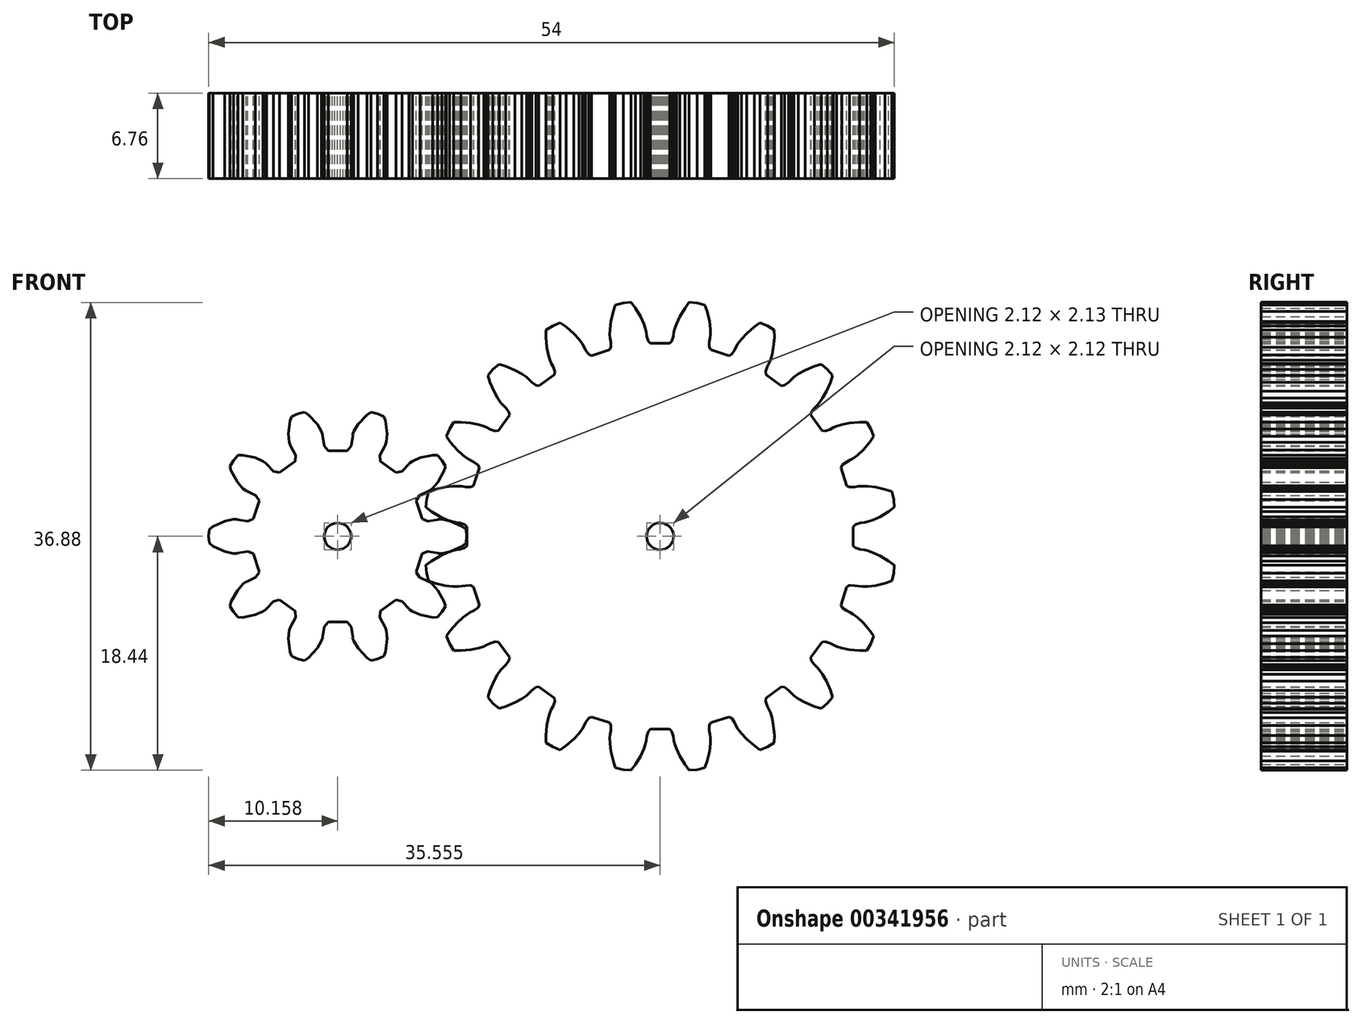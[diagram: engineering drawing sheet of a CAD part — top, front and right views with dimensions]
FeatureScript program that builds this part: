
annotation { "Feature Type Name" : "Feature", "Feature Type Description" : "" }
export const myFeature = defineFeature(function(context is Context, id is Id, definition is map)
    precondition{}
    {
        {
            var Q0;
            Q0=qCreatedBy(makeId("Front.planeOp"),FACE);
            var sketch = newSketch(context, id + "F0", { "sketchPlane" : qUnion([Q0])});
            skLineSegment(sketch, "E0", {"start": v(-16.87, -12) * mm, "end": v(-16.21, -11.23) * mm});
            skLineSegment(sketch, "E1", {"start": v(-16.21, -11.23) * mm, "end": v(-15.68, -10.36) * mm});
            skLineSegment(sketch, "E2", {"start": v(-15.68, -10.36) * mm, "end": v(-15.9, -9.67) * mm});
            skLineSegment(sketch, "E3", {"start": v(-15.9, -9.67) * mm, "end": v(-16.82, -8) * mm});
            skLineSegment(sketch, "E4", {"start": v(-16.82, -8) * mm, "end": v(-17.64, -7.07) * mm});
            skLineSegment(sketch, "E5", {"start": v(-17.64, -7.07) * mm, "end": v(-18.07, -6.75) * mm});
            skLineSegment(sketch, "E6", {"start": v(-18.07, -6.75) * mm, "end": v(-18.2, -6.72) * mm});
            skLineSegment(sketch, "E7", {"start": v(-18.2, -6.72) * mm, "end": v(-19.55, -6.05) * mm});
            skLineSegment(sketch, "E8", {"start": v(-19.55, -6.05) * mm, "end": v(-20.04, -5.27) * mm});
            skLineSegment(sketch, "E9", {"start": v(-20.04, -5.27) * mm, "end": v(-19.16, -2.57) * mm});
            skLineSegment(sketch, "E10", {"start": v(-19.16, -2.57) * mm, "end": v(-18.3, -2.22) * mm});
            skLineSegment(sketch, "E11", {"start": v(-18.3, -2.22) * mm, "end": v(-16.83, -2.48) * mm});
            skLineSegment(sketch, "E12", {"start": v(-16.83, -2.48) * mm, "end": v(-16.7, -2.53) * mm});
            skLineSegment(sketch, "E13", {"start": v(-16.7, -2.53) * mm, "end": v(-16.16, -2.52) * mm});
            skLineSegment(sketch, "E14", {"start": v(-16.16, -2.52) * mm, "end": v(-14.95, -2.24) * mm});
            skLineSegment(sketch, "E15", {"start": v(-14.95, -2.24) * mm, "end": v(-13.22, -1.44) * mm});
            skLineSegment(sketch, "E16", {"start": v(-13.22, -1.44) * mm, "end": v(-12.64, -1) * mm});
            skLineSegment(sketch, "E17", {"start": v(-12.64, -1) * mm, "end": v(-12.56, 0) * mm});
            skLineSegment(sketch, "E18", {"start": v(-12.56, 0) * mm, "end": v(-12.64, 1) * mm});
            skLineSegment(sketch, "E19", {"start": v(-12.64, 1) * mm, "end": v(-13.22, 1.44) * mm});
            skLineSegment(sketch, "E20", {"start": v(-13.22, 1.44) * mm, "end": v(-14.95, 2.24) * mm});
            skLineSegment(sketch, "E21", {"start": v(-14.95, 2.24) * mm, "end": v(-16.16, 2.52) * mm});
            skLineSegment(sketch, "E22", {"start": v(-16.16, 2.52) * mm, "end": v(-16.7, 2.53) * mm});
            skLineSegment(sketch, "E23", {"start": v(-16.7, 2.53) * mm, "end": v(-16.83, 2.48) * mm});
            skLineSegment(sketch, "E24", {"start": v(-16.83, 2.48) * mm, "end": v(-18.3, 2.22) * mm});
            skLineSegment(sketch, "E25", {"start": v(-18.3, 2.22) * mm, "end": v(-19.16, 2.57) * mm});
            skLineSegment(sketch, "E26", {"start": v(-19.16, 2.57) * mm, "end": v(-20.04, 5.27) * mm});
            skLineSegment(sketch, "E27", {"start": v(-20.04, 5.27) * mm, "end": v(-19.55, 6.05) * mm});
            skLineSegment(sketch, "E28", {"start": v(-19.55, 6.05) * mm, "end": v(-18.2, 6.72) * mm});
            skLineSegment(sketch, "E29", {"start": v(-18.2, 6.72) * mm, "end": v(-18.07, 6.75) * mm});
            skLineSegment(sketch, "E30", {"start": v(-18.07, 6.75) * mm, "end": v(-17.64, 7.07) * mm});
            skLineSegment(sketch, "E31", {"start": v(-17.64, 7.07) * mm, "end": v(-16.82, 8) * mm});
            skLineSegment(sketch, "E32", {"start": v(-16.82, 8) * mm, "end": v(-15.9, 9.67) * mm});
            skLineSegment(sketch, "E33", {"start": v(-15.9, 9.67) * mm, "end": v(-15.68, 10.36) * mm});
            skLineSegment(sketch, "E34", {"start": v(-15.68, 10.36) * mm, "end": v(-16.21, 11.23) * mm});
            skLineSegment(sketch, "E35", {"start": v(-16.21, 11.23) * mm, "end": v(-16.87, 12) * mm});
            skLineSegment(sketch, "E36", {"start": v(-16.87, 12) * mm, "end": v(-17.6, 12) * mm});
            skLineSegment(sketch, "E37", {"start": v(-17.6, 12) * mm, "end": v(-19.46, 11.64) * mm});
            skLineSegment(sketch, "E38", {"start": v(-19.46, 11.64) * mm, "end": v(-20.6, 11.15) * mm});
            skLineSegment(sketch, "E39", {"start": v(-20.6, 11.15) * mm, "end": v(-21.04, 10.84) * mm});
            skLineSegment(sketch, "E40", {"start": v(-21.04, 10.84) * mm, "end": v(-21.11, 10.72) * mm});
            skLineSegment(sketch, "E41", {"start": v(-21.11, 10.72) * mm, "end": v(-22.16, 9.65) * mm});
            skLineSegment(sketch, "E42", {"start": v(-22.16, 9.65) * mm, "end": v(-23.06, 9.43) * mm});
            skLineSegment(sketch, "E43", {"start": v(-23.06, 9.43) * mm, "end": v(-25.36, 11.1) * mm});
            skLineSegment(sketch, "E44", {"start": v(-25.36, 11.1) * mm, "end": v(-25.42, 12.02) * mm});
            skLineSegment(sketch, "E45", {"start": v(-25.42, 12.02) * mm, "end": v(-24.72, 13.35) * mm});
            skLineSegment(sketch, "E46", {"start": v(-24.72, 13.35) * mm, "end": v(-24.63, 13.45) * mm});
            skLineSegment(sketch, "E47", {"start": v(-24.63, 13.45) * mm, "end": v(-24.47, 13.96) * mm});
            skLineSegment(sketch, "E48", {"start": v(-24.47, 13.96) * mm, "end": v(-24.36, 15.2) * mm});
            skLineSegment(sketch, "E49", {"start": v(-24.36, 15.2) * mm, "end": v(-24.6, 17.1) * mm});
            skLineSegment(sketch, "E50", {"start": v(-24.6, 17.1) * mm, "end": v(-24.82, 17.78) * mm});
            skLineSegment(sketch, "E51", {"start": v(-24.82, 17.78) * mm, "end": v(-25.76, 18.16) * mm});
            skLineSegment(sketch, "E52", {"start": v(-25.76, 18.16) * mm, "end": v(-26.74, 18.4) * mm});
            skLineSegment(sketch, "E53", {"start": v(-26.74, 18.4) * mm, "end": v(-27.33, 17.98) * mm});
            skLineSegment(sketch, "E54", {"start": v(-27.33, 17.98) * mm, "end": v(-28.63, 16.59) * mm});
            skLineSegment(sketch, "E55", {"start": v(-28.63, 16.59) * mm, "end": v(-29.27, 15.52) * mm});
            skLineSegment(sketch, "E56", {"start": v(-29.27, 15.52) * mm, "end": v(-29.44, 15.01) * mm});
            skLineSegment(sketch, "E57", {"start": v(-29.44, 15.01) * mm, "end": v(-29.43, 14.88) * mm});
            skLineSegment(sketch, "E58", {"start": v(-29.43, 14.88) * mm, "end": v(-29.65, 13.4) * mm});
            skLineSegment(sketch, "E59", {"start": v(-29.65, 13.4) * mm, "end": v(-30.24, 12.68) * mm});
            skLineSegment(sketch, "E60", {"start": v(-30.24, 12.68) * mm, "end": v(-33.08, 12.68) * mm});
            skLineSegment(sketch, "E61", {"start": v(-33.08, 12.68) * mm, "end": v(-33.68, 13.4) * mm});
            skLineSegment(sketch, "E62", {"start": v(-33.68, 13.4) * mm, "end": v(-33.9, 14.88) * mm});
            skLineSegment(sketch, "E63", {"start": v(-33.9, 14.88) * mm, "end": v(-33.88, 15.01) * mm});
            skLineSegment(sketch, "E64", {"start": v(-33.88, 15.01) * mm, "end": v(-34.05, 15.52) * mm});
            skLineSegment(sketch, "E65", {"start": v(-34.05, 15.52) * mm, "end": v(-34.7, 16.59) * mm});
            skLineSegment(sketch, "E66", {"start": v(-34.7, 16.59) * mm, "end": v(-35.99, 17.98) * mm});
            skLineSegment(sketch, "E67", {"start": v(-35.99, 17.98) * mm, "end": v(-36.58, 18.4) * mm});
            skLineSegment(sketch, "E68", {"start": v(-36.58, 18.4) * mm, "end": v(-37.56, 18.16) * mm});
            skLineSegment(sketch, "E69", {"start": v(-37.56, 18.16) * mm, "end": v(-38.5, 17.78) * mm});
            skLineSegment(sketch, "E70", {"start": v(-38.5, 17.78) * mm, "end": v(-38.73, 17.1) * mm});
            skLineSegment(sketch, "E71", {"start": v(-38.73, 17.1) * mm, "end": v(-38.96, 15.2) * mm});
            skLineSegment(sketch, "E72", {"start": v(-38.96, 15.2) * mm, "end": v(-38.85, 13.96) * mm});
            skLineSegment(sketch, "E73", {"start": v(-38.85, 13.96) * mm, "end": v(-38.7, 13.45) * mm});
            skLineSegment(sketch, "E74", {"start": v(-38.7, 13.45) * mm, "end": v(-38.6, 13.35) * mm});
            skLineSegment(sketch, "E75", {"start": v(-38.6, 13.35) * mm, "end": v(-37.9, 12.02) * mm});
            skLineSegment(sketch, "E76", {"start": v(-37.9, 12.02) * mm, "end": v(-37.97, 11.1) * mm});
            skLineSegment(sketch, "E77", {"start": v(-37.97, 11.1) * mm, "end": v(-40.27, 9.43) * mm});
            skLineSegment(sketch, "E78", {"start": v(-40.27, 9.43) * mm, "end": v(-41.16, 9.65) * mm});
            skLineSegment(sketch, "E79", {"start": v(-41.16, 9.65) * mm, "end": v(-42.2, 10.72) * mm});
            skLineSegment(sketch, "E80", {"start": v(-42.2, 10.72) * mm, "end": v(-42.28, 10.84) * mm});
            skLineSegment(sketch, "E81", {"start": v(-42.28, 10.84) * mm, "end": v(-42.72, 11.15) * mm});
            skLineSegment(sketch, "E82", {"start": v(-42.72, 11.15) * mm, "end": v(-43.86, 11.64) * mm});
            skLineSegment(sketch, "E83", {"start": v(-43.86, 11.64) * mm, "end": v(-45.73, 12) * mm});
            skLineSegment(sketch, "E84", {"start": v(-45.73, 12) * mm, "end": v(-46.46, 12) * mm});
            skLineSegment(sketch, "E85", {"start": v(-46.46, 12) * mm, "end": v(-47.11, 11.23) * mm});
            skLineSegment(sketch, "E86", {"start": v(-47.11, 11.23) * mm, "end": v(-47.64, 10.36) * mm});
            skLineSegment(sketch, "E87", {"start": v(-47.64, 10.36) * mm, "end": v(-47.43, 9.67) * mm});
            skLineSegment(sketch, "E88", {"start": v(-47.43, 9.67) * mm, "end": v(-46.5, 8) * mm});
            skLineSegment(sketch, "E89", {"start": v(-46.5, 8) * mm, "end": v(-45.68, 7.07) * mm});
            skLineSegment(sketch, "E90", {"start": v(-45.68, 7.07) * mm, "end": v(-45.25, 6.75) * mm});
            skLineSegment(sketch, "E91", {"start": v(-45.25, 6.75) * mm, "end": v(-45.12, 6.72) * mm});
            skLineSegment(sketch, "E92", {"start": v(-45.12, 6.72) * mm, "end": v(-43.78, 6.05) * mm});
            skLineSegment(sketch, "E93", {"start": v(-43.78, 6.05) * mm, "end": v(-43.28, 5.27) * mm});
            skLineSegment(sketch, "E94", {"start": v(-43.28, 5.27) * mm, "end": v(-44.16, 2.57) * mm});
            skLineSegment(sketch, "E95", {"start": v(-44.16, 2.57) * mm, "end": v(-45.02, 2.22) * mm});
            skLineSegment(sketch, "E96", {"start": v(-45.02, 2.22) * mm, "end": v(-46.5, 2.48) * mm});
            skLineSegment(sketch, "E97", {"start": v(-46.5, 2.48) * mm, "end": v(-46.62, 2.53) * mm});
            skLineSegment(sketch, "E98", {"start": v(-46.62, 2.53) * mm, "end": v(-47.16, 2.52) * mm});
            skLineSegment(sketch, "E99", {"start": v(-47.16, 2.52) * mm, "end": v(-48.37, 2.24) * mm});
            skLineSegment(sketch, "E100", {"start": v(-48.37, 2.24) * mm, "end": v(-50.1, 1.44) * mm});
            skLineSegment(sketch, "E101", {"start": v(-50.1, 1.44) * mm, "end": v(-50.68, 1) * mm});
            skLineSegment(sketch, "E102", {"start": v(-50.68, 1) * mm, "end": v(-50.76, 0) * mm});
            skLineSegment(sketch, "E103", {"start": v(-50.76, 0) * mm, "end": v(-50.68, -1) * mm});
            skLineSegment(sketch, "E104", {"start": v(-50.68, -1) * mm, "end": v(-50.1, -1.44) * mm});
            skLineSegment(sketch, "E105", {"start": v(-50.1, -1.44) * mm, "end": v(-48.37, -2.24) * mm});
            skLineSegment(sketch, "E106", {"start": v(-48.37, -2.24) * mm, "end": v(-47.16, -2.52) * mm});
            skLineSegment(sketch, "E107", {"start": v(-47.16, -2.52) * mm, "end": v(-46.62, -2.53) * mm});
            skLineSegment(sketch, "E108", {"start": v(-46.62, -2.53) * mm, "end": v(-46.5, -2.48) * mm});
            skLineSegment(sketch, "E109", {"start": v(-46.5, -2.48) * mm, "end": v(-45.02, -2.22) * mm});
            skLineSegment(sketch, "E110", {"start": v(-45.02, -2.22) * mm, "end": v(-44.16, -2.57) * mm});
            skLineSegment(sketch, "E111", {"start": v(-44.16, -2.57) * mm, "end": v(-43.28, -5.27) * mm});
            skLineSegment(sketch, "E112", {"start": v(-43.28, -5.27) * mm, "end": v(-43.78, -6.05) * mm});
            skLineSegment(sketch, "E113", {"start": v(-43.78, -6.05) * mm, "end": v(-45.12, -6.72) * mm});
            skLineSegment(sketch, "E114", {"start": v(-45.12, -6.72) * mm, "end": v(-45.25, -6.75) * mm});
            skLineSegment(sketch, "E115", {"start": v(-45.25, -6.75) * mm, "end": v(-45.68, -7.07) * mm});
            skLineSegment(sketch, "E116", {"start": v(-45.68, -7.07) * mm, "end": v(-46.5, -8) * mm});
            skLineSegment(sketch, "E117", {"start": v(-46.5, -8) * mm, "end": v(-47.43, -9.67) * mm});
            skLineSegment(sketch, "E118", {"start": v(-47.43, -9.67) * mm, "end": v(-47.64, -10.36) * mm});
            skLineSegment(sketch, "E119", {"start": v(-47.64, -10.36) * mm, "end": v(-47.11, -11.23) * mm});
            skLineSegment(sketch, "E120", {"start": v(-47.11, -11.23) * mm, "end": v(-46.46, -12) * mm});
            skLineSegment(sketch, "E121", {"start": v(-46.46, -12) * mm, "end": v(-45.73, -12) * mm});
            skLineSegment(sketch, "E122", {"start": v(-45.73, -12) * mm, "end": v(-43.86, -11.64) * mm});
            skLineSegment(sketch, "E123", {"start": v(-43.86, -11.64) * mm, "end": v(-42.72, -11.15) * mm});
            skLineSegment(sketch, "E124", {"start": v(-42.72, -11.15) * mm, "end": v(-42.28, -10.84) * mm});
            skLineSegment(sketch, "E125", {"start": v(-42.28, -10.84) * mm, "end": v(-42.2, -10.72) * mm});
            skLineSegment(sketch, "E126", {"start": v(-42.2, -10.72) * mm, "end": v(-41.16, -9.65) * mm});
            skLineSegment(sketch, "E127", {"start": v(-41.16, -9.65) * mm, "end": v(-40.27, -9.43) * mm});
            skLineSegment(sketch, "E128", {"start": v(-40.27, -9.43) * mm, "end": v(-37.97, -11.1) * mm});
            skLineSegment(sketch, "E129", {"start": v(-37.97, -11.1) * mm, "end": v(-37.9, -12.02) * mm});
            skLineSegment(sketch, "E130", {"start": v(-37.9, -12.02) * mm, "end": v(-38.6, -13.35) * mm});
            skLineSegment(sketch, "E131", {"start": v(-38.6, -13.35) * mm, "end": v(-38.7, -13.45) * mm});
            skLineSegment(sketch, "E132", {"start": v(-38.7, -13.45) * mm, "end": v(-38.85, -13.96) * mm});
            skLineSegment(sketch, "E133", {"start": v(-38.85, -13.96) * mm, "end": v(-38.96, -15.2) * mm});
            skLineSegment(sketch, "E134", {"start": v(-38.96, -15.2) * mm, "end": v(-38.73, -17.1) * mm});
            skLineSegment(sketch, "E135", {"start": v(-38.73, -17.1) * mm, "end": v(-38.5, -17.78) * mm});
            skLineSegment(sketch, "E136", {"start": v(-38.5, -17.78) * mm, "end": v(-37.56, -18.16) * mm});
            skLineSegment(sketch, "E137", {"start": v(-37.56, -18.16) * mm, "end": v(-36.58, -18.4) * mm});
            skLineSegment(sketch, "E138", {"start": v(-36.58, -18.4) * mm, "end": v(-35.99, -17.98) * mm});
            skLineSegment(sketch, "E139", {"start": v(-35.99, -17.98) * mm, "end": v(-34.7, -16.59) * mm});
            skLineSegment(sketch, "E140", {"start": v(-34.7, -16.59) * mm, "end": v(-34.05, -15.52) * mm});
            skLineSegment(sketch, "E141", {"start": v(-34.05, -15.52) * mm, "end": v(-33.88, -15.01) * mm});
            skLineSegment(sketch, "E142", {"start": v(-33.88, -15.01) * mm, "end": v(-33.9, -14.88) * mm});
            skLineSegment(sketch, "E143", {"start": v(-33.9, -14.88) * mm, "end": v(-33.68, -13.4) * mm});
            skLineSegment(sketch, "E144", {"start": v(-33.68, -13.4) * mm, "end": v(-33.08, -12.68) * mm});
            skLineSegment(sketch, "E145", {"start": v(-33.08, -12.68) * mm, "end": v(-30.24, -12.68) * mm});
            skLineSegment(sketch, "E146", {"start": v(-30.24, -12.68) * mm, "end": v(-29.65, -13.4) * mm});
            skLineSegment(sketch, "E147", {"start": v(-29.65, -13.4) * mm, "end": v(-29.43, -14.88) * mm});
            skLineSegment(sketch, "E148", {"start": v(-29.43, -14.88) * mm, "end": v(-29.44, -15.01) * mm});
            skLineSegment(sketch, "E149", {"start": v(-29.44, -15.01) * mm, "end": v(-29.27, -15.52) * mm});
            skLineSegment(sketch, "E150", {"start": v(-29.27, -15.52) * mm, "end": v(-28.63, -16.59) * mm});
            skLineSegment(sketch, "E151", {"start": v(-28.63, -16.59) * mm, "end": v(-27.33, -17.98) * mm});
            skLineSegment(sketch, "E152", {"start": v(-27.33, -17.98) * mm, "end": v(-26.74, -18.4) * mm});
            skLineSegment(sketch, "E153", {"start": v(-26.74, -18.4) * mm, "end": v(-25.76, -18.16) * mm});
            skLineSegment(sketch, "E154", {"start": v(-25.76, -18.16) * mm, "end": v(-24.82, -17.78) * mm});
            skLineSegment(sketch, "E155", {"start": v(-24.82, -17.78) * mm, "end": v(-24.6, -17.1) * mm});
            skLineSegment(sketch, "E156", {"start": v(-24.6, -17.1) * mm, "end": v(-24.36, -15.2) * mm});
            skLineSegment(sketch, "E157", {"start": v(-24.36, -15.2) * mm, "end": v(-24.47, -13.96) * mm});
            skLineSegment(sketch, "E158", {"start": v(-24.47, -13.96) * mm, "end": v(-24.63, -13.45) * mm});
            skLineSegment(sketch, "E159", {"start": v(-24.63, -13.45) * mm, "end": v(-24.72, -13.35) * mm});
            skLineSegment(sketch, "E160", {"start": v(-24.72, -13.35) * mm, "end": v(-25.42, -12.02) * mm});
            skLineSegment(sketch, "E161", {"start": v(-25.42, -12.02) * mm, "end": v(-25.36, -11.1) * mm});
            skLineSegment(sketch, "E162", {"start": v(-25.36, -11.1) * mm, "end": v(-23.06, -9.43) * mm});
            skLineSegment(sketch, "E163", {"start": v(-23.06, -9.43) * mm, "end": v(-22.16, -9.65) * mm});
            skLineSegment(sketch, "E164", {"start": v(-22.16, -9.65) * mm, "end": v(-21.11, -10.72) * mm});
            skLineSegment(sketch, "E165", {"start": v(-21.11, -10.72) * mm, "end": v(-21.04, -10.84) * mm});
            skLineSegment(sketch, "E166", {"start": v(-21.04, -10.84) * mm, "end": v(-20.6, -11.15) * mm});
            skLineSegment(sketch, "E167", {"start": v(-20.6, -11.15) * mm, "end": v(-19.46, -11.64) * mm});
            skLineSegment(sketch, "E168", {"start": v(-19.46, -11.64) * mm, "end": v(-17.6, -12) * mm});
            skLineSegment(sketch, "E169", {"start": v(-17.6, -12) * mm, "end": v(-16.87, -12) * mm});
            skLineSegment(sketch, "E170", {"start": v(-31.25, -1.96) * mm, "end": v(-31.66, -2) * mm});
            skLineSegment(sketch, "E171", {"start": v(-31.66, -2) * mm, "end": v(-32.08, -1.96) * mm});
            skLineSegment(sketch, "E172", {"start": v(-32.08, -1.96) * mm, "end": v(-32.48, -1.83) * mm});
            skLineSegment(sketch, "E173", {"start": v(-32.48, -1.83) * mm, "end": v(-32.84, -1.62) * mm});
            skLineSegment(sketch, "E174", {"start": v(-32.84, -1.62) * mm, "end": v(-33.15, -1.34) * mm});
            skLineSegment(sketch, "E175", {"start": v(-33.15, -1.34) * mm, "end": v(-33.4, -1) * mm});
            skLineSegment(sketch, "E176", {"start": v(-33.4, -1) * mm, "end": v(-33.56, -0.62) * mm});
            skLineSegment(sketch, "E177", {"start": v(-33.56, -0.62) * mm, "end": v(-33.65, -0.2) * mm});
            skLineSegment(sketch, "E178", {"start": v(-33.65, -0.2) * mm, "end": v(-33.65, 0.2) * mm});
            skLineSegment(sketch, "E179", {"start": v(-33.65, 0.2) * mm, "end": v(-33.56, 0.62) * mm});
            skLineSegment(sketch, "E180", {"start": v(-33.56, 0.62) * mm, "end": v(-33.4, 1) * mm});
            skLineSegment(sketch, "E181", {"start": v(-33.4, 1) * mm, "end": v(-33.15, 1.34) * mm});
            skLineSegment(sketch, "E182", {"start": v(-33.15, 1.34) * mm, "end": v(-32.84, 1.62) * mm});
            skLineSegment(sketch, "E183", {"start": v(-32.84, 1.62) * mm, "end": v(-32.48, 1.83) * mm});
            skLineSegment(sketch, "E184", {"start": v(-32.48, 1.83) * mm, "end": v(-32.08, 1.96) * mm});
            skLineSegment(sketch, "E185", {"start": v(-32.08, 1.96) * mm, "end": v(-31.66, 2) * mm});
            skLineSegment(sketch, "E186", {"start": v(-31.66, 2) * mm, "end": v(-31.25, 1.96) * mm});
            skLineSegment(sketch, "E187", {"start": v(-31.25, 1.96) * mm, "end": v(-30.85, 1.83) * mm});
            skLineSegment(sketch, "E188", {"start": v(-30.85, 1.83) * mm, "end": v(-30.49, 1.62) * mm});
            skLineSegment(sketch, "E189", {"start": v(-30.49, 1.62) * mm, "end": v(-30.18, 1.34) * mm});
            skLineSegment(sketch, "E190", {"start": v(-30.18, 1.34) * mm, "end": v(-29.93, 1) * mm});
            skLineSegment(sketch, "E191", {"start": v(-29.93, 1) * mm, "end": v(-29.76, 0.62) * mm});
            skLineSegment(sketch, "E192", {"start": v(-29.76, 0.62) * mm, "end": v(-29.67, 0.2) * mm});
            skLineSegment(sketch, "E193", {"start": v(-29.67, 0.2) * mm, "end": v(-29.67, -0.2) * mm});
            skLineSegment(sketch, "E194", {"start": v(-29.67, -0.2) * mm, "end": v(-29.76, -0.62) * mm});
            skLineSegment(sketch, "E195", {"start": v(-29.76, -0.62) * mm, "end": v(-29.93, -1) * mm});
            skLineSegment(sketch, "E196", {"start": v(-29.93, -1) * mm, "end": v(-30.18, -1.34) * mm});
            skLineSegment(sketch, "E197", {"start": v(-30.18, -1.34) * mm, "end": v(-30.49, -1.62) * mm});
            skLineSegment(sketch, "E198", {"start": v(-30.49, -1.62) * mm, "end": v(-30.85, -1.83) * mm});
            skLineSegment(sketch, "E199", {"start": v(-30.85, -1.83) * mm, "end": v(-31.25, -1.96) * mm});
            skLineSegment(sketch, "E200", {"start": v(-18.22, 6.63) * mm, "end": v(-18.5, 5.48) * mm});
            skLineSegment(sketch, "E201", {"start": v(-18.5, 5.48) * mm, "end": v(-18.6, 4.3) * mm});
            skLineSegment(sketch, "E202", {"start": v(-18.6, 4.3) * mm, "end": v(-17.75, 3.67) * mm});
            skLineSegment(sketch, "E203", {"start": v(-17.75, 3.67) * mm, "end": v(-16.47, 2.9) * mm});
            skLineSegment(sketch, "E204", {"start": v(-16.47, 2.9) * mm, "end": v(-15.42, 2.41) * mm});
            skLineSegment(sketch, "E205", {"start": v(-15.42, 2.41) * mm, "end": v(-14.63, 2.15) * mm});
            skLineSegment(sketch, "E206", {"start": v(-14.63, 2.15) * mm, "end": v(-14.15, 2.03) * mm});
            skLineSegment(sketch, "E207", {"start": v(-14.15, 2.03) * mm, "end": v(-13.57, 1.96) * mm});
            skLineSegment(sketch, "E208", {"start": v(-13.57, 1.96) * mm, "end": v(-12.85, 1.74) * mm});
            skLineSegment(sketch, "E209", {"start": v(-12.85, 1.74) * mm, "end": v(-12.51, 1.42) * mm});
            skLineSegment(sketch, "E210", {"start": v(-12.51, 1.42) * mm, "end": v(-12.51, -1.42) * mm});
            skLineSegment(sketch, "E211", {"start": v(-12.51, -1.42) * mm, "end": v(-12.85, -1.74) * mm});
            skLineSegment(sketch, "E212", {"start": v(-12.85, -1.74) * mm, "end": v(-13.57, -1.96) * mm});
            skLineSegment(sketch, "E213", {"start": v(-13.57, -1.96) * mm, "end": v(-14.15, -2.03) * mm});
            skLineSegment(sketch, "E214", {"start": v(-14.15, -2.03) * mm, "end": v(-14.63, -2.15) * mm});
            skLineSegment(sketch, "E215", {"start": v(-14.63, -2.15) * mm, "end": v(-15.42, -2.41) * mm});
            skLineSegment(sketch, "E216", {"start": v(-15.42, -2.41) * mm, "end": v(-16.47, -2.9) * mm});
            skLineSegment(sketch, "E217", {"start": v(-16.47, -2.9) * mm, "end": v(-17.75, -3.67) * mm});
            skLineSegment(sketch, "E218", {"start": v(-17.75, -3.67) * mm, "end": v(-18.6, -4.3) * mm});
            skLineSegment(sketch, "E219", {"start": v(-18.6, -4.3) * mm, "end": v(-18.5, -5.48) * mm});
            skLineSegment(sketch, "E220", {"start": v(-18.5, -5.48) * mm, "end": v(-18.22, -6.63) * mm});
            skLineSegment(sketch, "E221", {"start": v(-18.22, -6.63) * mm, "end": v(-17.23, -6.97) * mm});
            skLineSegment(sketch, "E222", {"start": v(-17.23, -6.97) * mm, "end": v(-15.77, -7.3) * mm});
            skLineSegment(sketch, "E223", {"start": v(-15.77, -7.3) * mm, "end": v(-14.62, -7.44) * mm});
            skLineSegment(sketch, "E224", {"start": v(-14.62, -7.44) * mm, "end": v(-13.8, -7.45) * mm});
            skLineSegment(sketch, "E225", {"start": v(-13.8, -7.45) * mm, "end": v(-13.3, -7.4) * mm});
            skLineSegment(sketch, "E226", {"start": v(-13.3, -7.4) * mm, "end": v(-12.73, -7.3) * mm});
            skLineSegment(sketch, "E227", {"start": v(-12.73, -7.3) * mm, "end": v(-11.97, -7.29) * mm});
            skLineSegment(sketch, "E228", {"start": v(-11.97, -7.29) * mm, "end": v(-11.55, -7.49) * mm});
            skLineSegment(sketch, "E229", {"start": v(-11.55, -7.49) * mm, "end": v(-10.67, -10.19) * mm});
            skLineSegment(sketch, "E230", {"start": v(-10.67, -10.19) * mm, "end": v(-10.9, -10.6) * mm});
            skLineSegment(sketch, "E231", {"start": v(-10.9, -10.6) * mm, "end": v(-11.51, -11.03) * mm});
            skLineSegment(sketch, "E232", {"start": v(-11.51, -11.03) * mm, "end": v(-12.04, -11.28) * mm});
            skLineSegment(sketch, "E233", {"start": v(-12.04, -11.28) * mm, "end": v(-12.47, -11.53) * mm});
            skLineSegment(sketch, "E234", {"start": v(-12.47, -11.53) * mm, "end": v(-13.13, -12.03) * mm});
            skLineSegment(sketch, "E235", {"start": v(-13.13, -12.03) * mm, "end": v(-13.98, -12.82) * mm});
            skLineSegment(sketch, "E236", {"start": v(-13.98, -12.82) * mm, "end": v(-14.96, -13.94) * mm});
            skLineSegment(sketch, "E237", {"start": v(-14.96, -13.94) * mm, "end": v(-15.57, -14.8) * mm});
            skLineSegment(sketch, "E238", {"start": v(-15.57, -14.8) * mm, "end": v(-15.11, -15.9) * mm});
            skLineSegment(sketch, "E239", {"start": v(-15.11, -15.9) * mm, "end": v(-14.5, -16.9) * mm});
            skLineSegment(sketch, "E240", {"start": v(-14.5, -16.9) * mm, "end": v(-13.44, -16.92) * mm});
            skLineSegment(sketch, "E241", {"start": v(-13.44, -16.92) * mm, "end": v(-11.96, -16.79) * mm});
            skLineSegment(sketch, "E242", {"start": v(-11.96, -16.79) * mm, "end": v(-10.82, -16.56) * mm});
            skLineSegment(sketch, "E243", {"start": v(-10.82, -16.56) * mm, "end": v(-10.03, -16.32) * mm});
            skLineSegment(sketch, "E244", {"start": v(-10.03, -16.32) * mm, "end": v(-9.57, -16.12) * mm});
            skLineSegment(sketch, "E245", {"start": v(-9.57, -16.12) * mm, "end": v(-9.06, -15.84) * mm});
            skLineSegment(sketch, "E246", {"start": v(-9.06, -15.84) * mm, "end": v(-8.35, -15.6) * mm});
            skLineSegment(sketch, "E247", {"start": v(-8.35, -15.6) * mm, "end": v(-7.89, -15.66) * mm});
            skLineSegment(sketch, "E248", {"start": v(-7.89, -15.66) * mm, "end": v(-6.22, -17.96) * mm});
            skLineSegment(sketch, "E249", {"start": v(-6.22, -17.96) * mm, "end": v(-6.3, -18.42) * mm});
            skLineSegment(sketch, "E250", {"start": v(-6.3, -18.42) * mm, "end": v(-6.75, -19.02) * mm});
            skLineSegment(sketch, "E251", {"start": v(-6.75, -19.02) * mm, "end": v(-7.18, -19.42) * mm});
            skLineSegment(sketch, "E252", {"start": v(-7.18, -19.42) * mm, "end": v(-7.5, -19.8) * mm});
            skLineSegment(sketch, "E253", {"start": v(-7.5, -19.8) * mm, "end": v(-7.98, -20.47) * mm});
            skLineSegment(sketch, "E254", {"start": v(-7.98, -20.47) * mm, "end": v(-8.55, -21.48) * mm});
            skLineSegment(sketch, "E255", {"start": v(-8.55, -21.48) * mm, "end": v(-9.13, -22.85) * mm});
            skLineSegment(sketch, "E256", {"start": v(-9.13, -22.85) * mm, "end": v(-9.44, -23.86) * mm});
            skLineSegment(sketch, "E257", {"start": v(-9.44, -23.86) * mm, "end": v(-8.67, -24.76) * mm});
            skLineSegment(sketch, "E258", {"start": v(-8.67, -24.76) * mm, "end": v(-7.78, -25.53) * mm});
            skLineSegment(sketch, "E259", {"start": v(-7.78, -25.53) * mm, "end": v(-6.77, -25.22) * mm});
            skLineSegment(sketch, "E260", {"start": v(-6.77, -25.22) * mm, "end": v(-5.4, -24.63) * mm});
            skLineSegment(sketch, "E261", {"start": v(-5.4, -24.63) * mm, "end": v(-4.38, -24.07) * mm});
            skLineSegment(sketch, "E262", {"start": v(-4.38, -24.07) * mm, "end": v(-3.7, -23.59) * mm});
            skLineSegment(sketch, "E263", {"start": v(-3.7, -23.59) * mm, "end": v(-3.33, -23.26) * mm});
            skLineSegment(sketch, "E264", {"start": v(-3.33, -23.26) * mm, "end": v(-2.94, -22.84) * mm});
            skLineSegment(sketch, "E265", {"start": v(-2.94, -22.84) * mm, "end": v(-2.33, -22.39) * mm});
            skLineSegment(sketch, "E266", {"start": v(-2.33, -22.39) * mm, "end": v(-1.87, -22.3) * mm});
            skLineSegment(sketch, "E267", {"start": v(-1.87, -22.3) * mm, "end": v(0.42, -23.97) * mm});
            skLineSegment(sketch, "E268", {"start": v(0.42, -23.97) * mm, "end": v(0.48, -24.43) * mm});
            skLineSegment(sketch, "E269", {"start": v(0.48, -24.43) * mm, "end": v(0.24, -25.15) * mm});
            skLineSegment(sketch, "E270", {"start": v(0.24, -25.15) * mm, "end": v(-0.04, -25.65) * mm});
            skLineSegment(sketch, "E271", {"start": v(-0.04, -25.65) * mm, "end": v(-0.23, -26.11) * mm});
            skLineSegment(sketch, "E272", {"start": v(-0.23, -26.11) * mm, "end": v(-0.48, -26.9) * mm});
            skLineSegment(sketch, "E273", {"start": v(-0.48, -26.9) * mm, "end": v(-0.7, -28.04) * mm});
            skLineSegment(sketch, "E274", {"start": v(-0.7, -28.04) * mm, "end": v(-0.84, -29.53) * mm});
            skLineSegment(sketch, "E275", {"start": v(-0.84, -29.53) * mm, "end": v(-0.82, -30.58) * mm});
            skLineSegment(sketch, "E276", {"start": v(-0.82, -30.58) * mm, "end": v(0.19, -31.2) * mm});
            skLineSegment(sketch, "E277", {"start": v(0.19, -31.2) * mm, "end": v(1.28, -31.65) * mm});
            skLineSegment(sketch, "E278", {"start": v(1.28, -31.65) * mm, "end": v(2.14, -31.04) * mm});
            skLineSegment(sketch, "E279", {"start": v(2.14, -31.04) * mm, "end": v(3.27, -30.06) * mm});
            skLineSegment(sketch, "E280", {"start": v(3.27, -30.06) * mm, "end": v(4.05, -29.21) * mm});
            skLineSegment(sketch, "E281", {"start": v(4.05, -29.21) * mm, "end": v(4.55, -28.55) * mm});
            skLineSegment(sketch, "E282", {"start": v(4.55, -28.55) * mm, "end": v(4.8, -28.12) * mm});
            skLineSegment(sketch, "E283", {"start": v(4.8, -28.12) * mm, "end": v(5.05, -27.6) * mm});
            skLineSegment(sketch, "E284", {"start": v(5.05, -27.6) * mm, "end": v(5.49, -26.98) * mm});
            skLineSegment(sketch, "E285", {"start": v(5.49, -26.98) * mm, "end": v(5.9, -26.76) * mm});
            skLineSegment(sketch, "E286", {"start": v(5.9, -26.76) * mm, "end": v(8.6, -27.64) * mm});
            skLineSegment(sketch, "E287", {"start": v(8.6, -27.64) * mm, "end": v(8.8, -28.06) * mm});
            skLineSegment(sketch, "E288", {"start": v(8.8, -28.06) * mm, "end": v(8.79, -28.81) * mm});
            skLineSegment(sketch, "E289", {"start": v(8.79, -28.81) * mm, "end": v(8.68, -29.38) * mm});
            skLineSegment(sketch, "E290", {"start": v(8.68, -29.38) * mm, "end": v(8.63, -29.88) * mm});
            skLineSegment(sketch, "E291", {"start": v(8.63, -29.88) * mm, "end": v(8.65, -30.7) * mm});
            skLineSegment(sketch, "E292", {"start": v(8.65, -30.7) * mm, "end": v(8.78, -31.86) * mm});
            skLineSegment(sketch, "E293", {"start": v(8.78, -31.86) * mm, "end": v(9.12, -33.31) * mm});
            skLineSegment(sketch, "E294", {"start": v(9.12, -33.31) * mm, "end": v(9.46, -34.3) * mm});
            skLineSegment(sketch, "E295", {"start": v(9.46, -34.3) * mm, "end": v(10.6, -34.58) * mm});
            skLineSegment(sketch, "E296", {"start": v(10.6, -34.58) * mm, "end": v(11.79, -34.68) * mm});
            skLineSegment(sketch, "E297", {"start": v(11.79, -34.68) * mm, "end": v(12.42, -33.83) * mm});
            skLineSegment(sketch, "E298", {"start": v(12.42, -33.83) * mm, "end": v(13.18, -32.55) * mm});
            skLineSegment(sketch, "E299", {"start": v(13.18, -32.55) * mm, "end": v(13.67, -31.5) * mm});
            skLineSegment(sketch, "E300", {"start": v(13.67, -31.5) * mm, "end": v(13.94, -30.72) * mm});
            skLineSegment(sketch, "E301", {"start": v(13.94, -30.72) * mm, "end": v(14.05, -30.23) * mm});
            skLineSegment(sketch, "E302", {"start": v(14.05, -30.23) * mm, "end": v(14.12, -29.65) * mm});
            skLineSegment(sketch, "E303", {"start": v(14.12, -29.65) * mm, "end": v(14.35, -28.94) * mm});
            skLineSegment(sketch, "E304", {"start": v(14.35, -28.94) * mm, "end": v(14.66, -28.6) * mm});
            skLineSegment(sketch, "E305", {"start": v(14.66, -28.6) * mm, "end": v(17.5, -28.6) * mm});
            skLineSegment(sketch, "E306", {"start": v(17.5, -28.6) * mm, "end": v(17.82, -28.94) * mm});
            skLineSegment(sketch, "E307", {"start": v(17.82, -28.94) * mm, "end": v(18.05, -29.65) * mm});
            skLineSegment(sketch, "E308", {"start": v(18.05, -29.65) * mm, "end": v(18.12, -30.23) * mm});
            skLineSegment(sketch, "E309", {"start": v(18.12, -30.23) * mm, "end": v(18.23, -30.72) * mm});
            skLineSegment(sketch, "E310", {"start": v(18.23, -30.72) * mm, "end": v(18.5, -31.5) * mm});
            skLineSegment(sketch, "E311", {"start": v(18.5, -31.5) * mm, "end": v(18.99, -32.55) * mm});
            skLineSegment(sketch, "E312", {"start": v(18.99, -32.55) * mm, "end": v(19.75, -33.83) * mm});
            skLineSegment(sketch, "E313", {"start": v(19.75, -33.83) * mm, "end": v(20.38, -34.68) * mm});
            skLineSegment(sketch, "E314", {"start": v(20.38, -34.68) * mm, "end": v(21.56, -34.58) * mm});
            skLineSegment(sketch, "E315", {"start": v(21.56, -34.58) * mm, "end": v(22.71, -34.3) * mm});
            skLineSegment(sketch, "E316", {"start": v(22.71, -34.3) * mm, "end": v(23.05, -33.31) * mm});
            skLineSegment(sketch, "E317", {"start": v(23.05, -33.31) * mm, "end": v(23.38, -31.86) * mm});
            skLineSegment(sketch, "E318", {"start": v(23.38, -31.86) * mm, "end": v(23.52, -30.7) * mm});
            skLineSegment(sketch, "E319", {"start": v(23.52, -30.7) * mm, "end": v(23.54, -29.88) * mm});
            skLineSegment(sketch, "E320", {"start": v(23.54, -29.88) * mm, "end": v(23.5, -29.38) * mm});
            skLineSegment(sketch, "E321", {"start": v(23.5, -29.38) * mm, "end": v(23.38, -28.81) * mm});
            skLineSegment(sketch, "E322", {"start": v(23.38, -28.81) * mm, "end": v(23.37, -28.06) * mm});
            skLineSegment(sketch, "E323", {"start": v(23.37, -28.06) * mm, "end": v(23.57, -27.64) * mm});
            skLineSegment(sketch, "E324", {"start": v(23.57, -27.64) * mm, "end": v(26.27, -26.76) * mm});
            skLineSegment(sketch, "E325", {"start": v(26.27, -26.76) * mm, "end": v(26.68, -26.98) * mm});
            skLineSegment(sketch, "E326", {"start": v(26.68, -26.98) * mm, "end": v(27.12, -27.6) * mm});
            skLineSegment(sketch, "E327", {"start": v(27.12, -27.6) * mm, "end": v(27.36, -28.12) * mm});
            skLineSegment(sketch, "E328", {"start": v(27.36, -28.12) * mm, "end": v(27.62, -28.55) * mm});
            skLineSegment(sketch, "E329", {"start": v(27.62, -28.55) * mm, "end": v(28.12, -29.21) * mm});
            skLineSegment(sketch, "E330", {"start": v(28.12, -29.21) * mm, "end": v(28.9, -30.06) * mm});
            skLineSegment(sketch, "E331", {"start": v(28.9, -30.06) * mm, "end": v(30.03, -31.04) * mm});
            skLineSegment(sketch, "E332", {"start": v(30.03, -31.04) * mm, "end": v(30.89, -31.65) * mm});
            skLineSegment(sketch, "E333", {"start": v(30.89, -31.65) * mm, "end": v(31.98, -31.2) * mm});
            skLineSegment(sketch, "E334", {"start": v(31.98, -31.2) * mm, "end": v(32.99, -30.58) * mm});
            skLineSegment(sketch, "E335", {"start": v(32.99, -30.58) * mm, "end": v(33, -29.53) * mm});
            skLineSegment(sketch, "E336", {"start": v(33, -29.53) * mm, "end": v(32.87, -28.04) * mm});
            skLineSegment(sketch, "E337", {"start": v(32.87, -28.04) * mm, "end": v(32.65, -26.9) * mm});
            skLineSegment(sketch, "E338", {"start": v(32.65, -26.9) * mm, "end": v(32.4, -26.11) * mm});
            skLineSegment(sketch, "E339", {"start": v(32.4, -26.11) * mm, "end": v(32.2, -25.65) * mm});
            skLineSegment(sketch, "E340", {"start": v(32.2, -25.65) * mm, "end": v(31.93, -25.15) * mm});
            skLineSegment(sketch, "E341", {"start": v(31.93, -25.15) * mm, "end": v(31.69, -24.43) * mm});
            skLineSegment(sketch, "E342", {"start": v(31.69, -24.43) * mm, "end": v(31.74, -23.97) * mm});
            skLineSegment(sketch, "E343", {"start": v(31.74, -23.97) * mm, "end": v(34.04, -22.3) * mm});
            skLineSegment(sketch, "E344", {"start": v(34.04, -22.3) * mm, "end": v(34.5, -22.39) * mm});
            skLineSegment(sketch, "E345", {"start": v(34.5, -22.39) * mm, "end": v(35.1, -22.84) * mm});
            skLineSegment(sketch, "E346", {"start": v(35.1, -22.84) * mm, "end": v(35.5, -23.26) * mm});
            skLineSegment(sketch, "E347", {"start": v(35.5, -23.26) * mm, "end": v(35.88, -23.59) * mm});
            skLineSegment(sketch, "E348", {"start": v(35.88, -23.59) * mm, "end": v(36.55, -24.07) * mm});
            skLineSegment(sketch, "E349", {"start": v(36.55, -24.07) * mm, "end": v(37.57, -24.63) * mm});
            skLineSegment(sketch, "E350", {"start": v(37.57, -24.63) * mm, "end": v(38.94, -25.22) * mm});
            skLineSegment(sketch, "E351", {"start": v(38.94, -25.22) * mm, "end": v(39.94, -25.53) * mm});
            skLineSegment(sketch, "E352", {"start": v(39.94, -25.53) * mm, "end": v(40.84, -24.76) * mm});
            skLineSegment(sketch, "E353", {"start": v(40.84, -24.76) * mm, "end": v(41.61, -23.86) * mm});
            skLineSegment(sketch, "E354", {"start": v(41.61, -23.86) * mm, "end": v(41.3, -22.85) * mm});
            skLineSegment(sketch, "E355", {"start": v(41.3, -22.85) * mm, "end": v(40.72, -21.48) * mm});
            skLineSegment(sketch, "E356", {"start": v(40.72, -21.48) * mm, "end": v(40.15, -20.47) * mm});
            skLineSegment(sketch, "E357", {"start": v(40.15, -20.47) * mm, "end": v(39.67, -19.8) * mm});
            skLineSegment(sketch, "E358", {"start": v(39.67, -19.8) * mm, "end": v(39.35, -19.42) * mm});
            skLineSegment(sketch, "E359", {"start": v(39.35, -19.42) * mm, "end": v(38.92, -19.02) * mm});
            skLineSegment(sketch, "E360", {"start": v(38.92, -19.02) * mm, "end": v(38.47, -18.42) * mm});
            skLineSegment(sketch, "E361", {"start": v(38.47, -18.42) * mm, "end": v(38.39, -17.96) * mm});
            skLineSegment(sketch, "E362", {"start": v(38.39, -17.96) * mm, "end": v(40.06, -15.66) * mm});
            skLineSegment(sketch, "E363", {"start": v(40.06, -15.66) * mm, "end": v(40.52, -15.6) * mm});
            skLineSegment(sketch, "E364", {"start": v(40.52, -15.6) * mm, "end": v(41.23, -15.84) * mm});
            skLineSegment(sketch, "E365", {"start": v(41.23, -15.84) * mm, "end": v(41.74, -16.12) * mm});
            skLineSegment(sketch, "E366", {"start": v(41.74, -16.12) * mm, "end": v(42.2, -16.32) * mm});
            skLineSegment(sketch, "E367", {"start": v(42.2, -16.32) * mm, "end": v(42.99, -16.56) * mm});
            skLineSegment(sketch, "E368", {"start": v(42.99, -16.56) * mm, "end": v(44.13, -16.79) * mm});
            skLineSegment(sketch, "E369", {"start": v(44.13, -16.79) * mm, "end": v(45.61, -16.92) * mm});
            skLineSegment(sketch, "E370", {"start": v(45.61, -16.92) * mm, "end": v(46.66, -16.9) * mm});
            skLineSegment(sketch, "E371", {"start": v(46.66, -16.9) * mm, "end": v(47.28, -15.9) * mm});
            skLineSegment(sketch, "E372", {"start": v(47.28, -15.9) * mm, "end": v(47.73, -14.8) * mm});
            skLineSegment(sketch, "E373", {"start": v(47.73, -14.8) * mm, "end": v(47.13, -13.94) * mm});
            skLineSegment(sketch, "E374", {"start": v(47.13, -13.94) * mm, "end": v(46.15, -12.82) * mm});
            skLineSegment(sketch, "E375", {"start": v(46.15, -12.82) * mm, "end": v(45.3, -12.03) * mm});
            skLineSegment(sketch, "E376", {"start": v(45.3, -12.03) * mm, "end": v(44.64, -11.53) * mm});
            skLineSegment(sketch, "E377", {"start": v(44.64, -11.53) * mm, "end": v(44.2, -11.28) * mm});
            skLineSegment(sketch, "E378", {"start": v(44.2, -11.28) * mm, "end": v(43.68, -11.03) * mm});
            skLineSegment(sketch, "E379", {"start": v(43.68, -11.03) * mm, "end": v(43.07, -10.6) * mm});
            skLineSegment(sketch, "E380", {"start": v(43.07, -10.6) * mm, "end": v(42.84, -10.19) * mm});
            skLineSegment(sketch, "E381", {"start": v(42.84, -10.19) * mm, "end": v(43.72, -7.49) * mm});
            skLineSegment(sketch, "E382", {"start": v(43.72, -7.49) * mm, "end": v(44.14, -7.29) * mm});
            skLineSegment(sketch, "E383", {"start": v(44.14, -7.29) * mm, "end": v(44.9, -7.3) * mm});
            skLineSegment(sketch, "E384", {"start": v(44.9, -7.3) * mm, "end": v(45.46, -7.4) * mm});
            skLineSegment(sketch, "E385", {"start": v(45.46, -7.4) * mm, "end": v(45.96, -7.45) * mm});
            skLineSegment(sketch, "E386", {"start": v(45.96, -7.45) * mm, "end": v(46.8, -7.44) * mm});
            skLineSegment(sketch, "E387", {"start": v(46.8, -7.44) * mm, "end": v(47.94, -7.3) * mm});
            skLineSegment(sketch, "E388", {"start": v(47.94, -7.3) * mm, "end": v(49.4, -6.97) * mm});
            skLineSegment(sketch, "E389", {"start": v(49.4, -6.97) * mm, "end": v(50.4, -6.63) * mm});
            skLineSegment(sketch, "E390", {"start": v(50.4, -6.63) * mm, "end": v(50.67, -5.48) * mm});
            skLineSegment(sketch, "E391", {"start": v(50.67, -5.48) * mm, "end": v(50.76, -4.3) * mm});
            skLineSegment(sketch, "E392", {"start": v(50.76, -4.3) * mm, "end": v(49.92, -3.67) * mm});
            skLineSegment(sketch, "E393", {"start": v(49.92, -3.67) * mm, "end": v(48.64, -2.9) * mm});
            skLineSegment(sketch, "E394", {"start": v(48.64, -2.9) * mm, "end": v(47.59, -2.41) * mm});
            skLineSegment(sketch, "E395", {"start": v(47.59, -2.41) * mm, "end": v(46.8, -2.15) * mm});
            skLineSegment(sketch, "E396", {"start": v(46.8, -2.15) * mm, "end": v(46.32, -2.03) * mm});
            skLineSegment(sketch, "E397", {"start": v(46.32, -2.03) * mm, "end": v(45.74, -1.96) * mm});
            skLineSegment(sketch, "E398", {"start": v(45.74, -1.96) * mm, "end": v(45.02, -1.74) * mm});
            skLineSegment(sketch, "E399", {"start": v(45.02, -1.74) * mm, "end": v(44.68, -1.42) * mm});
            skLineSegment(sketch, "E400", {"start": v(44.68, -1.42) * mm, "end": v(44.68, 1.42) * mm});
            skLineSegment(sketch, "E401", {"start": v(44.68, 1.42) * mm, "end": v(45.02, 1.74) * mm});
            skLineSegment(sketch, "E402", {"start": v(45.02, 1.74) * mm, "end": v(45.74, 1.96) * mm});
            skLineSegment(sketch, "E403", {"start": v(45.74, 1.96) * mm, "end": v(46.32, 2.03) * mm});
            skLineSegment(sketch, "E404", {"start": v(46.32, 2.03) * mm, "end": v(46.8, 2.15) * mm});
            skLineSegment(sketch, "E405", {"start": v(46.8, 2.15) * mm, "end": v(47.59, 2.41) * mm});
            skLineSegment(sketch, "E406", {"start": v(47.59, 2.41) * mm, "end": v(48.64, 2.9) * mm});
            skLineSegment(sketch, "E407", {"start": v(48.64, 2.9) * mm, "end": v(49.92, 3.67) * mm});
            skLineSegment(sketch, "E408", {"start": v(49.92, 3.67) * mm, "end": v(50.76, 4.3) * mm});
            skLineSegment(sketch, "E409", {"start": v(50.76, 4.3) * mm, "end": v(50.67, 5.48) * mm});
            skLineSegment(sketch, "E410", {"start": v(50.67, 5.48) * mm, "end": v(50.4, 6.63) * mm});
            skLineSegment(sketch, "E411", {"start": v(50.4, 6.63) * mm, "end": v(49.4, 6.97) * mm});
            skLineSegment(sketch, "E412", {"start": v(49.4, 6.97) * mm, "end": v(47.94, 7.3) * mm});
            skLineSegment(sketch, "E413", {"start": v(47.94, 7.3) * mm, "end": v(46.8, 7.44) * mm});
            skLineSegment(sketch, "E414", {"start": v(46.8, 7.44) * mm, "end": v(45.96, 7.45) * mm});
            skLineSegment(sketch, "E415", {"start": v(45.96, 7.45) * mm, "end": v(45.46, 7.4) * mm});
            skLineSegment(sketch, "E416", {"start": v(45.46, 7.4) * mm, "end": v(44.9, 7.3) * mm});
            skLineSegment(sketch, "E417", {"start": v(44.9, 7.3) * mm, "end": v(44.14, 7.29) * mm});
            skLineSegment(sketch, "E418", {"start": v(44.14, 7.29) * mm, "end": v(43.72, 7.49) * mm});
            skLineSegment(sketch, "E419", {"start": v(43.72, 7.49) * mm, "end": v(42.84, 10.19) * mm});
            skLineSegment(sketch, "E420", {"start": v(42.84, 10.19) * mm, "end": v(43.07, 10.6) * mm});
            skLineSegment(sketch, "E421", {"start": v(43.07, 10.6) * mm, "end": v(43.68, 11.03) * mm});
            skLineSegment(sketch, "E422", {"start": v(43.68, 11.03) * mm, "end": v(44.2, 11.28) * mm});
            skLineSegment(sketch, "E423", {"start": v(44.2, 11.28) * mm, "end": v(44.64, 11.53) * mm});
            skLineSegment(sketch, "E424", {"start": v(44.64, 11.53) * mm, "end": v(45.3, 12.03) * mm});
            skLineSegment(sketch, "E425", {"start": v(45.3, 12.03) * mm, "end": v(46.15, 12.82) * mm});
            skLineSegment(sketch, "E426", {"start": v(46.15, 12.82) * mm, "end": v(47.13, 13.94) * mm});
            skLineSegment(sketch, "E427", {"start": v(47.13, 13.94) * mm, "end": v(47.73, 14.8) * mm});
            skLineSegment(sketch, "E428", {"start": v(47.73, 14.8) * mm, "end": v(47.28, 15.9) * mm});
            skLineSegment(sketch, "E429", {"start": v(47.28, 15.9) * mm, "end": v(46.66, 16.9) * mm});
            skLineSegment(sketch, "E430", {"start": v(46.66, 16.9) * mm, "end": v(45.61, 16.92) * mm});
            skLineSegment(sketch, "E431", {"start": v(45.61, 16.92) * mm, "end": v(44.13, 16.79) * mm});
            skLineSegment(sketch, "E432", {"start": v(44.13, 16.79) * mm, "end": v(42.99, 16.56) * mm});
            skLineSegment(sketch, "E433", {"start": v(42.99, 16.56) * mm, "end": v(42.2, 16.32) * mm});
            skLineSegment(sketch, "E434", {"start": v(42.2, 16.32) * mm, "end": v(41.74, 16.12) * mm});
            skLineSegment(sketch, "E435", {"start": v(41.74, 16.12) * mm, "end": v(41.23, 15.84) * mm});
            skLineSegment(sketch, "E436", {"start": v(41.23, 15.84) * mm, "end": v(40.52, 15.6) * mm});
            skLineSegment(sketch, "E437", {"start": v(40.52, 15.6) * mm, "end": v(40.06, 15.66) * mm});
            skLineSegment(sketch, "E438", {"start": v(40.06, 15.66) * mm, "end": v(38.39, 17.96) * mm});
            skLineSegment(sketch, "E439", {"start": v(38.39, 17.96) * mm, "end": v(38.47, 18.42) * mm});
            skLineSegment(sketch, "E440", {"start": v(38.47, 18.42) * mm, "end": v(38.92, 19.02) * mm});
            skLineSegment(sketch, "E441", {"start": v(38.92, 19.02) * mm, "end": v(39.35, 19.42) * mm});
            skLineSegment(sketch, "E442", {"start": v(39.35, 19.42) * mm, "end": v(39.67, 19.8) * mm});
            skLineSegment(sketch, "E443", {"start": v(39.67, 19.8) * mm, "end": v(40.15, 20.47) * mm});
            skLineSegment(sketch, "E444", {"start": v(40.15, 20.47) * mm, "end": v(40.72, 21.48) * mm});
            skLineSegment(sketch, "E445", {"start": v(40.72, 21.48) * mm, "end": v(41.3, 22.85) * mm});
            skLineSegment(sketch, "E446", {"start": v(41.3, 22.85) * mm, "end": v(41.61, 23.86) * mm});
            skLineSegment(sketch, "E447", {"start": v(41.61, 23.86) * mm, "end": v(40.84, 24.76) * mm});
            skLineSegment(sketch, "E448", {"start": v(40.84, 24.76) * mm, "end": v(39.94, 25.53) * mm});
            skLineSegment(sketch, "E449", {"start": v(39.94, 25.53) * mm, "end": v(38.94, 25.22) * mm});
            skLineSegment(sketch, "E450", {"start": v(38.94, 25.22) * mm, "end": v(37.57, 24.63) * mm});
            skLineSegment(sketch, "E451", {"start": v(37.57, 24.63) * mm, "end": v(36.55, 24.07) * mm});
            skLineSegment(sketch, "E452", {"start": v(36.55, 24.07) * mm, "end": v(35.88, 23.59) * mm});
            skLineSegment(sketch, "E453", {"start": v(35.88, 23.59) * mm, "end": v(35.5, 23.26) * mm});
            skLineSegment(sketch, "E454", {"start": v(35.5, 23.26) * mm, "end": v(35.1, 22.84) * mm});
            skLineSegment(sketch, "E455", {"start": v(35.1, 22.84) * mm, "end": v(34.5, 22.39) * mm});
            skLineSegment(sketch, "E456", {"start": v(34.5, 22.39) * mm, "end": v(34.04, 22.3) * mm});
            skLineSegment(sketch, "E457", {"start": v(34.04, 22.3) * mm, "end": v(31.74, 23.97) * mm});
            skLineSegment(sketch, "E458", {"start": v(31.74, 23.97) * mm, "end": v(31.69, 24.43) * mm});
            skLineSegment(sketch, "E459", {"start": v(31.69, 24.43) * mm, "end": v(31.93, 25.15) * mm});
            skLineSegment(sketch, "E460", {"start": v(31.93, 25.15) * mm, "end": v(32.2, 25.65) * mm});
            skLineSegment(sketch, "E461", {"start": v(32.2, 25.65) * mm, "end": v(32.4, 26.11) * mm});
            skLineSegment(sketch, "E462", {"start": v(32.4, 26.11) * mm, "end": v(32.65, 26.9) * mm});
            skLineSegment(sketch, "E463", {"start": v(32.65, 26.9) * mm, "end": v(32.87, 28.04) * mm});
            skLineSegment(sketch, "E464", {"start": v(32.87, 28.04) * mm, "end": v(33, 29.53) * mm});
            skLineSegment(sketch, "E465", {"start": v(33, 29.53) * mm, "end": v(32.99, 30.58) * mm});
            skLineSegment(sketch, "E466", {"start": v(32.99, 30.58) * mm, "end": v(31.98, 31.2) * mm});
            skLineSegment(sketch, "E467", {"start": v(31.98, 31.2) * mm, "end": v(30.89, 31.65) * mm});
            skLineSegment(sketch, "E468", {"start": v(30.89, 31.65) * mm, "end": v(30.03, 31.04) * mm});
            skLineSegment(sketch, "E469", {"start": v(30.03, 31.04) * mm, "end": v(28.9, 30.06) * mm});
            skLineSegment(sketch, "E470", {"start": v(28.9, 30.06) * mm, "end": v(28.12, 29.21) * mm});
            skLineSegment(sketch, "E471", {"start": v(28.12, 29.21) * mm, "end": v(27.62, 28.55) * mm});
            skLineSegment(sketch, "E472", {"start": v(27.62, 28.55) * mm, "end": v(27.36, 28.12) * mm});
            skLineSegment(sketch, "E473", {"start": v(27.36, 28.12) * mm, "end": v(27.12, 27.6) * mm});
            skLineSegment(sketch, "E474", {"start": v(27.12, 27.6) * mm, "end": v(26.68, 26.98) * mm});
            skLineSegment(sketch, "E475", {"start": v(26.68, 26.98) * mm, "end": v(26.27, 26.76) * mm});
            skLineSegment(sketch, "E476", {"start": v(26.27, 26.76) * mm, "end": v(23.57, 27.64) * mm});
            skLineSegment(sketch, "E477", {"start": v(23.57, 27.64) * mm, "end": v(23.37, 28.06) * mm});
            skLineSegment(sketch, "E478", {"start": v(23.37, 28.06) * mm, "end": v(23.38, 28.81) * mm});
            skLineSegment(sketch, "E479", {"start": v(23.38, 28.81) * mm, "end": v(23.5, 29.38) * mm});
            skLineSegment(sketch, "E480", {"start": v(23.5, 29.38) * mm, "end": v(23.54, 29.88) * mm});
            skLineSegment(sketch, "E481", {"start": v(23.54, 29.88) * mm, "end": v(23.52, 30.7) * mm});
            skLineSegment(sketch, "E482", {"start": v(23.52, 30.7) * mm, "end": v(23.38, 31.86) * mm});
            skLineSegment(sketch, "E483", {"start": v(23.38, 31.86) * mm, "end": v(23.05, 33.31) * mm});
            skLineSegment(sketch, "E484", {"start": v(23.05, 33.31) * mm, "end": v(22.71, 34.3) * mm});
            skLineSegment(sketch, "E485", {"start": v(22.71, 34.3) * mm, "end": v(21.56, 34.58) * mm});
            skLineSegment(sketch, "E486", {"start": v(21.56, 34.58) * mm, "end": v(20.38, 34.68) * mm});
            skLineSegment(sketch, "E487", {"start": v(20.38, 34.68) * mm, "end": v(19.75, 33.83) * mm});
            skLineSegment(sketch, "E488", {"start": v(19.75, 33.83) * mm, "end": v(18.99, 32.55) * mm});
            skLineSegment(sketch, "E489", {"start": v(18.99, 32.55) * mm, "end": v(18.5, 31.5) * mm});
            skLineSegment(sketch, "E490", {"start": v(18.5, 31.5) * mm, "end": v(18.23, 30.72) * mm});
            skLineSegment(sketch, "E491", {"start": v(18.23, 30.72) * mm, "end": v(18.12, 30.23) * mm});
            skLineSegment(sketch, "E492", {"start": v(18.12, 30.23) * mm, "end": v(18.05, 29.65) * mm});
            skLineSegment(sketch, "E493", {"start": v(18.05, 29.65) * mm, "end": v(17.82, 28.94) * mm});
            skLineSegment(sketch, "E494", {"start": v(17.82, 28.94) * mm, "end": v(17.5, 28.6) * mm});
            skLineSegment(sketch, "E495", {"start": v(17.5, 28.6) * mm, "end": v(14.66, 28.6) * mm});
            skLineSegment(sketch, "E496", {"start": v(14.66, 28.6) * mm, "end": v(14.35, 28.94) * mm});
            skLineSegment(sketch, "E497", {"start": v(14.35, 28.94) * mm, "end": v(14.12, 29.65) * mm});
            skLineSegment(sketch, "E498", {"start": v(14.12, 29.65) * mm, "end": v(14.05, 30.23) * mm});
            skLineSegment(sketch, "E499", {"start": v(14.05, 30.23) * mm, "end": v(13.94, 30.72) * mm});
            skLineSegment(sketch, "E500", {"start": v(13.94, 30.72) * mm, "end": v(13.67, 31.5) * mm});
            skLineSegment(sketch, "E501", {"start": v(13.67, 31.5) * mm, "end": v(13.18, 32.55) * mm});
            skLineSegment(sketch, "E502", {"start": v(13.18, 32.55) * mm, "end": v(12.42, 33.83) * mm});
            skLineSegment(sketch, "E503", {"start": v(12.42, 33.83) * mm, "end": v(11.79, 34.68) * mm});
            skLineSegment(sketch, "E504", {"start": v(11.79, 34.68) * mm, "end": v(10.6, 34.58) * mm});
            skLineSegment(sketch, "E505", {"start": v(10.6, 34.58) * mm, "end": v(9.46, 34.3) * mm});
            skLineSegment(sketch, "E506", {"start": v(9.46, 34.3) * mm, "end": v(9.12, 33.31) * mm});
            skLineSegment(sketch, "E507", {"start": v(9.12, 33.31) * mm, "end": v(8.78, 31.86) * mm});
            skLineSegment(sketch, "E508", {"start": v(8.78, 31.86) * mm, "end": v(8.65, 30.7) * mm});
            skLineSegment(sketch, "E509", {"start": v(8.65, 30.7) * mm, "end": v(8.63, 29.88) * mm});
            skLineSegment(sketch, "E510", {"start": v(8.63, 29.88) * mm, "end": v(8.68, 29.38) * mm});
            skLineSegment(sketch, "E511", {"start": v(8.68, 29.38) * mm, "end": v(8.79, 28.81) * mm});
            skLineSegment(sketch, "E512", {"start": v(8.79, 28.81) * mm, "end": v(8.8, 28.06) * mm});
            skLineSegment(sketch, "E513", {"start": v(8.8, 28.06) * mm, "end": v(8.6, 27.64) * mm});
            skLineSegment(sketch, "E514", {"start": v(8.6, 27.64) * mm, "end": v(5.9, 26.76) * mm});
            skLineSegment(sketch, "E515", {"start": v(5.9, 26.76) * mm, "end": v(5.49, 26.98) * mm});
            skLineSegment(sketch, "E516", {"start": v(5.49, 26.98) * mm, "end": v(5.05, 27.6) * mm});
            skLineSegment(sketch, "E517", {"start": v(5.05, 27.6) * mm, "end": v(4.8, 28.12) * mm});
            skLineSegment(sketch, "E518", {"start": v(4.8, 28.12) * mm, "end": v(4.55, 28.55) * mm});
            skLineSegment(sketch, "E519", {"start": v(4.55, 28.55) * mm, "end": v(4.05, 29.21) * mm});
            skLineSegment(sketch, "E520", {"start": v(4.05, 29.21) * mm, "end": v(3.27, 30.06) * mm});
            skLineSegment(sketch, "E521", {"start": v(3.27, 30.06) * mm, "end": v(2.14, 31.04) * mm});
            skLineSegment(sketch, "E522", {"start": v(2.14, 31.04) * mm, "end": v(1.28, 31.65) * mm});
            skLineSegment(sketch, "E523", {"start": v(1.28, 31.65) * mm, "end": v(0.19, 31.2) * mm});
            skLineSegment(sketch, "E524", {"start": v(0.19, 31.2) * mm, "end": v(-0.82, 30.58) * mm});
            skLineSegment(sketch, "E525", {"start": v(-0.82, 30.58) * mm, "end": v(-0.84, 29.53) * mm});
            skLineSegment(sketch, "E526", {"start": v(-0.84, 29.53) * mm, "end": v(-0.7, 28.04) * mm});
            skLineSegment(sketch, "E527", {"start": v(-0.7, 28.04) * mm, "end": v(-0.48, 26.9) * mm});
            skLineSegment(sketch, "E528", {"start": v(-0.48, 26.9) * mm, "end": v(-0.23, 26.11) * mm});
            skLineSegment(sketch, "E529", {"start": v(-0.23, 26.11) * mm, "end": v(-0.04, 25.65) * mm});
            skLineSegment(sketch, "E530", {"start": v(-0.04, 25.65) * mm, "end": v(0.24, 25.15) * mm});
            skLineSegment(sketch, "E531", {"start": v(0.24, 25.15) * mm, "end": v(0.48, 24.43) * mm});
            skLineSegment(sketch, "E532", {"start": v(0.48, 24.43) * mm, "end": v(0.42, 23.97) * mm});
            skLineSegment(sketch, "E533", {"start": v(0.42, 23.97) * mm, "end": v(-1.87, 22.3) * mm});
            skLineSegment(sketch, "E534", {"start": v(-1.87, 22.3) * mm, "end": v(-2.33, 22.39) * mm});
            skLineSegment(sketch, "E535", {"start": v(-2.33, 22.39) * mm, "end": v(-2.94, 22.84) * mm});
            skLineSegment(sketch, "E536", {"start": v(-2.94, 22.84) * mm, "end": v(-3.33, 23.26) * mm});
            skLineSegment(sketch, "E537", {"start": v(-3.33, 23.26) * mm, "end": v(-3.7, 23.59) * mm});
            skLineSegment(sketch, "E538", {"start": v(-3.7, 23.59) * mm, "end": v(-4.38, 24.07) * mm});
            skLineSegment(sketch, "E539", {"start": v(-4.38, 24.07) * mm, "end": v(-5.4, 24.63) * mm});
            skLineSegment(sketch, "E540", {"start": v(-5.4, 24.63) * mm, "end": v(-6.77, 25.22) * mm});
            skLineSegment(sketch, "E541", {"start": v(-6.77, 25.22) * mm, "end": v(-7.78, 25.53) * mm});
            skLineSegment(sketch, "E542", {"start": v(-7.78, 25.53) * mm, "end": v(-8.67, 24.76) * mm});
            skLineSegment(sketch, "E543", {"start": v(-8.67, 24.76) * mm, "end": v(-9.44, 23.86) * mm});
            skLineSegment(sketch, "E544", {"start": v(-9.44, 23.86) * mm, "end": v(-9.13, 22.85) * mm});
            skLineSegment(sketch, "E545", {"start": v(-9.13, 22.85) * mm, "end": v(-8.55, 21.48) * mm});
            skLineSegment(sketch, "E546", {"start": v(-8.55, 21.48) * mm, "end": v(-7.98, 20.47) * mm});
            skLineSegment(sketch, "E547", {"start": v(-7.98, 20.47) * mm, "end": v(-7.5, 19.8) * mm});
            skLineSegment(sketch, "E548", {"start": v(-7.5, 19.8) * mm, "end": v(-7.18, 19.42) * mm});
            skLineSegment(sketch, "E549", {"start": v(-7.18, 19.42) * mm, "end": v(-6.75, 19.02) * mm});
            skLineSegment(sketch, "E550", {"start": v(-6.75, 19.02) * mm, "end": v(-6.3, 18.42) * mm});
            skLineSegment(sketch, "E551", {"start": v(-6.3, 18.42) * mm, "end": v(-6.22, 17.96) * mm});
            skLineSegment(sketch, "E552", {"start": v(-6.22, 17.96) * mm, "end": v(-7.89, 15.66) * mm});
            skLineSegment(sketch, "E553", {"start": v(-7.89, 15.66) * mm, "end": v(-8.35, 15.6) * mm});
            skLineSegment(sketch, "E554", {"start": v(-8.35, 15.6) * mm, "end": v(-9.06, 15.84) * mm});
            skLineSegment(sketch, "E555", {"start": v(-9.06, 15.84) * mm, "end": v(-9.57, 16.12) * mm});
            skLineSegment(sketch, "E556", {"start": v(-9.57, 16.12) * mm, "end": v(-10.03, 16.32) * mm});
            skLineSegment(sketch, "E557", {"start": v(-10.03, 16.32) * mm, "end": v(-10.82, 16.56) * mm});
            skLineSegment(sketch, "E558", {"start": v(-10.82, 16.56) * mm, "end": v(-11.96, 16.79) * mm});
            skLineSegment(sketch, "E559", {"start": v(-11.96, 16.79) * mm, "end": v(-13.44, 16.92) * mm});
            skLineSegment(sketch, "E560", {"start": v(-13.44, 16.92) * mm, "end": v(-14.5, 16.9) * mm});
            skLineSegment(sketch, "E561", {"start": v(-14.5, 16.9) * mm, "end": v(-15.11, 15.9) * mm});
            skLineSegment(sketch, "E562", {"start": v(-15.11, 15.9) * mm, "end": v(-15.57, 14.8) * mm});
            skLineSegment(sketch, "E563", {"start": v(-15.57, 14.8) * mm, "end": v(-14.96, 13.94) * mm});
            skLineSegment(sketch, "E564", {"start": v(-14.96, 13.94) * mm, "end": v(-13.98, 12.82) * mm});
            skLineSegment(sketch, "E565", {"start": v(-13.98, 12.82) * mm, "end": v(-13.13, 12.03) * mm});
            skLineSegment(sketch, "E566", {"start": v(-13.13, 12.03) * mm, "end": v(-12.47, 11.53) * mm});
            skLineSegment(sketch, "E567", {"start": v(-12.47, 11.53) * mm, "end": v(-12.04, 11.28) * mm});
            skLineSegment(sketch, "E568", {"start": v(-12.04, 11.28) * mm, "end": v(-11.51, 11.03) * mm});
            skLineSegment(sketch, "E569", {"start": v(-11.51, 11.03) * mm, "end": v(-10.9, 10.6) * mm});
            skLineSegment(sketch, "E570", {"start": v(-10.9, 10.6) * mm, "end": v(-10.67, 10.19) * mm});
            skLineSegment(sketch, "E571", {"start": v(-10.67, 10.19) * mm, "end": v(-11.55, 7.49) * mm});
            skLineSegment(sketch, "E572", {"start": v(-11.55, 7.49) * mm, "end": v(-11.97, 7.29) * mm});
            skLineSegment(sketch, "E573", {"start": v(-11.97, 7.29) * mm, "end": v(-12.73, 7.3) * mm});
            skLineSegment(sketch, "E574", {"start": v(-12.73, 7.3) * mm, "end": v(-13.3, 7.4) * mm});
            skLineSegment(sketch, "E575", {"start": v(-13.3, 7.4) * mm, "end": v(-13.8, 7.45) * mm});
            skLineSegment(sketch, "E576", {"start": v(-13.8, 7.45) * mm, "end": v(-14.62, 7.44) * mm});
            skLineSegment(sketch, "E577", {"start": v(-14.62, 7.44) * mm, "end": v(-15.77, 7.3) * mm});
            skLineSegment(sketch, "E578", {"start": v(-15.77, 7.3) * mm, "end": v(-17.23, 6.97) * mm});
            skLineSegment(sketch, "E579", {"start": v(-17.23, 6.97) * mm, "end": v(-18.22, 6.63) * mm});
            skLineSegment(sketch, "E580", {"start": v(15.37, 1.87) * mm, "end": v(15.77, 1.98) * mm});
            skLineSegment(sketch, "E581", {"start": v(15.77, 1.98) * mm, "end": v(16.19, 2) * mm});
            skLineSegment(sketch, "E582", {"start": v(16.19, 2) * mm, "end": v(16.6, 1.93) * mm});
            skLineSegment(sketch, "E583", {"start": v(16.6, 1.93) * mm, "end": v(17, 1.78) * mm});
            skLineSegment(sketch, "E584", {"start": v(17, 1.78) * mm, "end": v(17.34, 1.55) * mm});
            skLineSegment(sketch, "E585", {"start": v(17.34, 1.55) * mm, "end": v(17.64, 1.26) * mm});
            skLineSegment(sketch, "E586", {"start": v(17.64, 1.26) * mm, "end": v(17.87, 0.9) * mm});
            skLineSegment(sketch, "E587", {"start": v(17.87, 0.9) * mm, "end": v(18.02, 0.52) * mm});
            skLineSegment(sketch, "E588", {"start": v(18.02, 0.52) * mm, "end": v(18.08, 0.1) * mm});
            skLineSegment(sketch, "E589", {"start": v(18.08, 0.1) * mm, "end": v(18.06, -0.31) * mm});
            skLineSegment(sketch, "E590", {"start": v(18.06, -0.31) * mm, "end": v(17.95, -0.72) * mm});
            skLineSegment(sketch, "E591", {"start": v(17.95, -0.72) * mm, "end": v(17.76, -1.09) * mm});
            skLineSegment(sketch, "E592", {"start": v(17.76, -1.09) * mm, "end": v(17.5, -1.41) * mm});
            skLineSegment(sketch, "E593", {"start": v(17.5, -1.41) * mm, "end": v(17.17, -1.68) * mm});
            skLineSegment(sketch, "E594", {"start": v(17.17, -1.68) * mm, "end": v(16.8, -1.87) * mm});
            skLineSegment(sketch, "E595", {"start": v(16.8, -1.87) * mm, "end": v(16.4, -1.98) * mm});
            skLineSegment(sketch, "E596", {"start": v(16.4, -1.98) * mm, "end": v(15.98, -2) * mm});
            skLineSegment(sketch, "E597", {"start": v(15.98, -2) * mm, "end": v(15.57, -1.93) * mm});
            skLineSegment(sketch, "E598", {"start": v(15.57, -1.93) * mm, "end": v(15.18, -1.78) * mm});
            skLineSegment(sketch, "E599", {"start": v(15.18, -1.78) * mm, "end": v(14.83, -1.55) * mm});
            skLineSegment(sketch, "E600", {"start": v(14.83, -1.55) * mm, "end": v(14.53, -1.26) * mm});
            skLineSegment(sketch, "E601", {"start": v(14.53, -1.26) * mm, "end": v(14.3, -0.9) * mm});
            skLineSegment(sketch, "E602", {"start": v(14.3, -0.9) * mm, "end": v(14.15, -0.52) * mm});
            skLineSegment(sketch, "E603", {"start": v(14.15, -0.52) * mm, "end": v(14.09, -0.1) * mm});
            skLineSegment(sketch, "E604", {"start": v(14.09, -0.1) * mm, "end": v(14.1, 0.31) * mm});
            skLineSegment(sketch, "E605", {"start": v(14.1, 0.31) * mm, "end": v(14.22, 0.72) * mm});
            skLineSegment(sketch, "E606", {"start": v(14.22, 0.72) * mm, "end": v(14.4, 1.09) * mm});
            skLineSegment(sketch, "E607", {"start": v(14.4, 1.09) * mm, "end": v(14.67, 1.41) * mm});
            skLineSegment(sketch, "E608", {"start": v(14.67, 1.41) * mm, "end": v(15, 1.68) * mm});
            skLineSegment(sketch, "E609", {"start": v(15, 1.68) * mm, "end": v(15.37, 1.87) * mm});
            skSolve(sketch);
        }
        {
            var Q0;
            Q0=makeQuery(id+"F0.imprint","IMPRINT",FACE,{"disambiguationData":[TD([[makeQuery(id+"F0.imprint","IMPRINT",EDGE,{"derivedFrom":sQuery(id+"F0.wireOp",EDGE,"E0")}),1.0]])]});
            var Q1;
            Q1=makeQuery(id+"F0.imprint","IMPRINT",FACE,{"disambiguationData":[TD([[makeQuery(id+"F0.imprint","IMPRINT",EDGE,{"derivedFrom":sQuery(id+"F0.wireOp",EDGE,"E200")}),1.0]])]});
            extrude(context, id + "F1", {"entities" : qUnion([Q0, Q1]), "depth" : 12.7 * mm});
        }
        {
            var Q0;
            Q0=makeQuery(id+"F1.opExtrude","CAP_FACE",FACE,{"disambiguationData":[OSD([sQuery(id+"F0.wireOp",EDGE,"E200"),sQuery(id+"F0.wireOp",EDGE,"E201"),sQuery(id+"F0.wireOp",EDGE,"E202"),sQuery(id+"F0.wireOp",EDGE,"E203"),sQuery(id+"F0.wireOp",EDGE,"E204"),sQuery(id+"F0.wireOp",EDGE,"E205"),sQuery(id+"F0.wireOp",EDGE,"E206"),sQuery(id+"F0.wireOp",EDGE,"E207"),sQuery(id+"F0.wireOp",EDGE,"E208"),sQuery(id+"F0.wireOp",EDGE,"E209"),sQuery(id+"F0.wireOp",EDGE,"E210"),sQuery(id+"F0.wireOp",EDGE,"E211"),sQuery(id+"F0.wireOp",EDGE,"E212"),sQuery(id+"F0.wireOp",EDGE,"E213"),sQuery(id+"F0.wireOp",EDGE,"E214"),sQuery(id+"F0.wireOp",EDGE,"E215"),sQuery(id+"F0.wireOp",EDGE,"E216"),sQuery(id+"F0.wireOp",EDGE,"E217"),sQuery(id+"F0.wireOp",EDGE,"E218"),sQuery(id+"F0.wireOp",EDGE,"E219"),sQuery(id+"F0.wireOp",EDGE,"E220"),sQuery(id+"F0.wireOp",EDGE,"E221"),sQuery(id+"F0.wireOp",EDGE,"E222"),sQuery(id+"F0.wireOp",EDGE,"E223"),sQuery(id+"F0.wireOp",EDGE,"E224"),sQuery(id+"F0.wireOp",EDGE,"E225"),sQuery(id+"F0.wireOp",EDGE,"E226"),sQuery(id+"F0.wireOp",EDGE,"E227"),sQuery(id+"F0.wireOp",EDGE,"E228"),sQuery(id+"F0.wireOp",EDGE,"E229"),sQuery(id+"F0.wireOp",EDGE,"E230"),sQuery(id+"F0.wireOp",EDGE,"E231"),sQuery(id+"F0.wireOp",EDGE,"E232"),sQuery(id+"F0.wireOp",EDGE,"E233"),sQuery(id+"F0.wireOp",EDGE,"E234"),sQuery(id+"F0.wireOp",EDGE,"E235"),sQuery(id+"F0.wireOp",EDGE,"E236"),sQuery(id+"F0.wireOp",EDGE,"E237"),sQuery(id+"F0.wireOp",EDGE,"E238"),sQuery(id+"F0.wireOp",EDGE,"E239"),sQuery(id+"F0.wireOp",EDGE,"E240"),sQuery(id+"F0.wireOp",EDGE,"E241"),sQuery(id+"F0.wireOp",EDGE,"E242"),sQuery(id+"F0.wireOp",EDGE,"E243"),sQuery(id+"F0.wireOp",EDGE,"E244"),sQuery(id+"F0.wireOp",EDGE,"E245"),sQuery(id+"F0.wireOp",EDGE,"E246"),sQuery(id+"F0.wireOp",EDGE,"E247"),sQuery(id+"F0.wireOp",EDGE,"E248"),sQuery(id+"F0.wireOp",EDGE,"E249"),sQuery(id+"F0.wireOp",EDGE,"E250"),sQuery(id+"F0.wireOp",EDGE,"E251"),sQuery(id+"F0.wireOp",EDGE,"E252"),sQuery(id+"F0.wireOp",EDGE,"E253"),sQuery(id+"F0.wireOp",EDGE,"E254"),sQuery(id+"F0.wireOp",EDGE,"E255"),sQuery(id+"F0.wireOp",EDGE,"E256"),sQuery(id+"F0.wireOp",EDGE,"E257"),sQuery(id+"F0.wireOp",EDGE,"E258"),sQuery(id+"F0.wireOp",EDGE,"E259"),sQuery(id+"F0.wireOp",EDGE,"E260"),sQuery(id+"F0.wireOp",EDGE,"E261"),sQuery(id+"F0.wireOp",EDGE,"E262"),sQuery(id+"F0.wireOp",EDGE,"E263"),sQuery(id+"F0.wireOp",EDGE,"E264"),sQuery(id+"F0.wireOp",EDGE,"E265"),sQuery(id+"F0.wireOp",EDGE,"E266"),sQuery(id+"F0.wireOp",EDGE,"E267"),sQuery(id+"F0.wireOp",EDGE,"E268"),sQuery(id+"F0.wireOp",EDGE,"E269"),sQuery(id+"F0.wireOp",EDGE,"E270"),sQuery(id+"F0.wireOp",EDGE,"E271"),sQuery(id+"F0.wireOp",EDGE,"E272"),sQuery(id+"F0.wireOp",EDGE,"E273"),sQuery(id+"F0.wireOp",EDGE,"E274"),sQuery(id+"F0.wireOp",EDGE,"E275"),sQuery(id+"F0.wireOp",EDGE,"E276"),sQuery(id+"F0.wireOp",EDGE,"E277"),sQuery(id+"F0.wireOp",EDGE,"E278"),sQuery(id+"F0.wireOp",EDGE,"E279"),sQuery(id+"F0.wireOp",EDGE,"E280"),sQuery(id+"F0.wireOp",EDGE,"E281"),sQuery(id+"F0.wireOp",EDGE,"E282"),sQuery(id+"F0.wireOp",EDGE,"E283"),sQuery(id+"F0.wireOp",EDGE,"E284"),sQuery(id+"F0.wireOp",EDGE,"E285"),sQuery(id+"F0.wireOp",EDGE,"E286"),sQuery(id+"F0.wireOp",EDGE,"E287"),sQuery(id+"F0.wireOp",EDGE,"E288"),sQuery(id+"F0.wireOp",EDGE,"E289"),sQuery(id+"F0.wireOp",EDGE,"E290"),sQuery(id+"F0.wireOp",EDGE,"E291"),sQuery(id+"F0.wireOp",EDGE,"E292"),sQuery(id+"F0.wireOp",EDGE,"E293"),sQuery(id+"F0.wireOp",EDGE,"E294"),sQuery(id+"F0.wireOp",EDGE,"E295"),sQuery(id+"F0.wireOp",EDGE,"E296"),sQuery(id+"F0.wireOp",EDGE,"E297"),sQuery(id+"F0.wireOp",EDGE,"E298"),sQuery(id+"F0.wireOp",EDGE,"E299"),sQuery(id+"F0.wireOp",EDGE,"E300"),sQuery(id+"F0.wireOp",EDGE,"E301"),sQuery(id+"F0.wireOp",EDGE,"E302"),sQuery(id+"F0.wireOp",EDGE,"E303"),sQuery(id+"F0.wireOp",EDGE,"E304"),sQuery(id+"F0.wireOp",EDGE,"E305"),sQuery(id+"F0.wireOp",EDGE,"E306"),sQuery(id+"F0.wireOp",EDGE,"E307"),sQuery(id+"F0.wireOp",EDGE,"E308"),sQuery(id+"F0.wireOp",EDGE,"E309"),sQuery(id+"F0.wireOp",EDGE,"E310"),sQuery(id+"F0.wireOp",EDGE,"E311"),sQuery(id+"F0.wireOp",EDGE,"E312"),sQuery(id+"F0.wireOp",EDGE,"E313"),sQuery(id+"F0.wireOp",EDGE,"E314"),sQuery(id+"F0.wireOp",EDGE,"E315"),sQuery(id+"F0.wireOp",EDGE,"E316"),sQuery(id+"F0.wireOp",EDGE,"E317"),sQuery(id+"F0.wireOp",EDGE,"E318"),sQuery(id+"F0.wireOp",EDGE,"E319"),sQuery(id+"F0.wireOp",EDGE,"E320"),sQuery(id+"F0.wireOp",EDGE,"E321"),sQuery(id+"F0.wireOp",EDGE,"E322"),sQuery(id+"F0.wireOp",EDGE,"E323"),sQuery(id+"F0.wireOp",EDGE,"E324"),sQuery(id+"F0.wireOp",EDGE,"E325"),sQuery(id+"F0.wireOp",EDGE,"E326"),sQuery(id+"F0.wireOp",EDGE,"E327"),sQuery(id+"F0.wireOp",EDGE,"E328"),sQuery(id+"F0.wireOp",EDGE,"E329"),sQuery(id+"F0.wireOp",EDGE,"E330"),sQuery(id+"F0.wireOp",EDGE,"E331"),sQuery(id+"F0.wireOp",EDGE,"E332"),sQuery(id+"F0.wireOp",EDGE,"E333"),sQuery(id+"F0.wireOp",EDGE,"E334"),sQuery(id+"F0.wireOp",EDGE,"E335"),sQuery(id+"F0.wireOp",EDGE,"E336"),sQuery(id+"F0.wireOp",EDGE,"E337"),sQuery(id+"F0.wireOp",EDGE,"E338"),sQuery(id+"F0.wireOp",EDGE,"E339"),sQuery(id+"F0.wireOp",EDGE,"E340"),sQuery(id+"F0.wireOp",EDGE,"E341"),sQuery(id+"F0.wireOp",EDGE,"E342"),sQuery(id+"F0.wireOp",EDGE,"E343"),sQuery(id+"F0.wireOp",EDGE,"E344"),sQuery(id+"F0.wireOp",EDGE,"E345"),sQuery(id+"F0.wireOp",EDGE,"E346"),sQuery(id+"F0.wireOp",EDGE,"E347"),sQuery(id+"F0.wireOp",EDGE,"E348"),sQuery(id+"F0.wireOp",EDGE,"E349"),sQuery(id+"F0.wireOp",EDGE,"E350"),sQuery(id+"F0.wireOp",EDGE,"E351"),sQuery(id+"F0.wireOp",EDGE,"E352"),sQuery(id+"F0.wireOp",EDGE,"E353"),sQuery(id+"F0.wireOp",EDGE,"E354"),sQuery(id+"F0.wireOp",EDGE,"E355"),sQuery(id+"F0.wireOp",EDGE,"E356"),sQuery(id+"F0.wireOp",EDGE,"E357"),sQuery(id+"F0.wireOp",EDGE,"E358"),sQuery(id+"F0.wireOp",EDGE,"E359"),sQuery(id+"F0.wireOp",EDGE,"E360"),sQuery(id+"F0.wireOp",EDGE,"E361"),sQuery(id+"F0.wireOp",EDGE,"E362"),sQuery(id+"F0.wireOp",EDGE,"E363"),sQuery(id+"F0.wireOp",EDGE,"E364"),sQuery(id+"F0.wireOp",EDGE,"E365"),sQuery(id+"F0.wireOp",EDGE,"E366"),sQuery(id+"F0.wireOp",EDGE,"E367"),sQuery(id+"F0.wireOp",EDGE,"E368"),sQuery(id+"F0.wireOp",EDGE,"E369"),sQuery(id+"F0.wireOp",EDGE,"E370"),sQuery(id+"F0.wireOp",EDGE,"E371"),sQuery(id+"F0.wireOp",EDGE,"E372"),sQuery(id+"F0.wireOp",EDGE,"E373"),sQuery(id+"F0.wireOp",EDGE,"E374"),sQuery(id+"F0.wireOp",EDGE,"E375"),sQuery(id+"F0.wireOp",EDGE,"E376"),sQuery(id+"F0.wireOp",EDGE,"E377"),sQuery(id+"F0.wireOp",EDGE,"E378"),sQuery(id+"F0.wireOp",EDGE,"E379"),sQuery(id+"F0.wireOp",EDGE,"E380"),sQuery(id+"F0.wireOp",EDGE,"E381"),sQuery(id+"F0.wireOp",EDGE,"E382"),sQuery(id+"F0.wireOp",EDGE,"E383"),sQuery(id+"F0.wireOp",EDGE,"E384"),sQuery(id+"F0.wireOp",EDGE,"E385"),sQuery(id+"F0.wireOp",EDGE,"E386"),sQuery(id+"F0.wireOp",EDGE,"E387"),sQuery(id+"F0.wireOp",EDGE,"E388"),sQuery(id+"F0.wireOp",EDGE,"E389"),sQuery(id+"F0.wireOp",EDGE,"E390"),sQuery(id+"F0.wireOp",EDGE,"E391"),sQuery(id+"F0.wireOp",EDGE,"E392"),sQuery(id+"F0.wireOp",EDGE,"E393"),sQuery(id+"F0.wireOp",EDGE,"E394"),sQuery(id+"F0.wireOp",EDGE,"E395"),sQuery(id+"F0.wireOp",EDGE,"E396"),sQuery(id+"F0.wireOp",EDGE,"E397"),sQuery(id+"F0.wireOp",EDGE,"E398"),sQuery(id+"F0.wireOp",EDGE,"E399"),sQuery(id+"F0.wireOp",EDGE,"E400"),sQuery(id+"F0.wireOp",EDGE,"E401"),sQuery(id+"F0.wireOp",EDGE,"E402"),sQuery(id+"F0.wireOp",EDGE,"E403"),sQuery(id+"F0.wireOp",EDGE,"E404"),sQuery(id+"F0.wireOp",EDGE,"E405"),sQuery(id+"F0.wireOp",EDGE,"E406"),sQuery(id+"F0.wireOp",EDGE,"E407"),sQuery(id+"F0.wireOp",EDGE,"E408"),sQuery(id+"F0.wireOp",EDGE,"E409"),sQuery(id+"F0.wireOp",EDGE,"E410"),sQuery(id+"F0.wireOp",EDGE,"E411"),sQuery(id+"F0.wireOp",EDGE,"E412"),sQuery(id+"F0.wireOp",EDGE,"E413"),sQuery(id+"F0.wireOp",EDGE,"E414"),sQuery(id+"F0.wireOp",EDGE,"E415"),sQuery(id+"F0.wireOp",EDGE,"E416"),sQuery(id+"F0.wireOp",EDGE,"E417"),sQuery(id+"F0.wireOp",EDGE,"E418"),sQuery(id+"F0.wireOp",EDGE,"E419"),sQuery(id+"F0.wireOp",EDGE,"E420"),sQuery(id+"F0.wireOp",EDGE,"E421"),sQuery(id+"F0.wireOp",EDGE,"E422"),sQuery(id+"F0.wireOp",EDGE,"E423"),sQuery(id+"F0.wireOp",EDGE,"E424"),sQuery(id+"F0.wireOp",EDGE,"E425"),sQuery(id+"F0.wireOp",EDGE,"E426"),sQuery(id+"F0.wireOp",EDGE,"E427"),sQuery(id+"F0.wireOp",EDGE,"E428"),sQuery(id+"F0.wireOp",EDGE,"E429"),sQuery(id+"F0.wireOp",EDGE,"E430"),sQuery(id+"F0.wireOp",EDGE,"E431"),sQuery(id+"F0.wireOp",EDGE,"E432"),sQuery(id+"F0.wireOp",EDGE,"E433"),sQuery(id+"F0.wireOp",EDGE,"E434"),sQuery(id+"F0.wireOp",EDGE,"E435"),sQuery(id+"F0.wireOp",EDGE,"E436"),sQuery(id+"F0.wireOp",EDGE,"E437"),sQuery(id+"F0.wireOp",EDGE,"E438"),sQuery(id+"F0.wireOp",EDGE,"E439"),sQuery(id+"F0.wireOp",EDGE,"E440"),sQuery(id+"F0.wireOp",EDGE,"E441"),sQuery(id+"F0.wireOp",EDGE,"E442"),sQuery(id+"F0.wireOp",EDGE,"E443"),sQuery(id+"F0.wireOp",EDGE,"E444"),sQuery(id+"F0.wireOp",EDGE,"E445"),sQuery(id+"F0.wireOp",EDGE,"E446"),sQuery(id+"F0.wireOp",EDGE,"E447"),sQuery(id+"F0.wireOp",EDGE,"E448"),sQuery(id+"F0.wireOp",EDGE,"E449"),sQuery(id+"F0.wireOp",EDGE,"E450"),sQuery(id+"F0.wireOp",EDGE,"E451"),sQuery(id+"F0.wireOp",EDGE,"E452"),sQuery(id+"F0.wireOp",EDGE,"E453"),sQuery(id+"F0.wireOp",EDGE,"E454"),sQuery(id+"F0.wireOp",EDGE,"E455"),sQuery(id+"F0.wireOp",EDGE,"E456"),sQuery(id+"F0.wireOp",EDGE,"E457"),sQuery(id+"F0.wireOp",EDGE,"E458"),sQuery(id+"F0.wireOp",EDGE,"E459"),sQuery(id+"F0.wireOp",EDGE,"E460"),sQuery(id+"F0.wireOp",EDGE,"E461"),sQuery(id+"F0.wireOp",EDGE,"E462"),sQuery(id+"F0.wireOp",EDGE,"E463"),sQuery(id+"F0.wireOp",EDGE,"E464"),sQuery(id+"F0.wireOp",EDGE,"E465"),sQuery(id+"F0.wireOp",EDGE,"E466"),sQuery(id+"F0.wireOp",EDGE,"E467"),sQuery(id+"F0.wireOp",EDGE,"E468"),sQuery(id+"F0.wireOp",EDGE,"E469"),sQuery(id+"F0.wireOp",EDGE,"E470"),sQuery(id+"F0.wireOp",EDGE,"E471"),sQuery(id+"F0.wireOp",EDGE,"E472"),sQuery(id+"F0.wireOp",EDGE,"E473"),sQuery(id+"F0.wireOp",EDGE,"E474"),sQuery(id+"F0.wireOp",EDGE,"E475"),sQuery(id+"F0.wireOp",EDGE,"E476"),sQuery(id+"F0.wireOp",EDGE,"E477"),sQuery(id+"F0.wireOp",EDGE,"E478"),sQuery(id+"F0.wireOp",EDGE,"E479"),sQuery(id+"F0.wireOp",EDGE,"E480"),sQuery(id+"F0.wireOp",EDGE,"E481"),sQuery(id+"F0.wireOp",EDGE,"E482"),sQuery(id+"F0.wireOp",EDGE,"E483"),sQuery(id+"F0.wireOp",EDGE,"E484"),sQuery(id+"F0.wireOp",EDGE,"E485"),sQuery(id+"F0.wireOp",EDGE,"E486"),sQuery(id+"F0.wireOp",EDGE,"E487"),sQuery(id+"F0.wireOp",EDGE,"E488"),sQuery(id+"F0.wireOp",EDGE,"E489"),sQuery(id+"F0.wireOp",EDGE,"E490"),sQuery(id+"F0.wireOp",EDGE,"E491"),sQuery(id+"F0.wireOp",EDGE,"E492"),sQuery(id+"F0.wireOp",EDGE,"E493"),sQuery(id+"F0.wireOp",EDGE,"E494"),sQuery(id+"F0.wireOp",EDGE,"E495"),sQuery(id+"F0.wireOp",EDGE,"E496"),sQuery(id+"F0.wireOp",EDGE,"E497"),sQuery(id+"F0.wireOp",EDGE,"E498"),sQuery(id+"F0.wireOp",EDGE,"E499"),sQuery(id+"F0.wireOp",EDGE,"E500"),sQuery(id+"F0.wireOp",EDGE,"E501"),sQuery(id+"F0.wireOp",EDGE,"E502"),sQuery(id+"F0.wireOp",EDGE,"E503"),sQuery(id+"F0.wireOp",EDGE,"E504"),sQuery(id+"F0.wireOp",EDGE,"E505"),sQuery(id+"F0.wireOp",EDGE,"E506"),sQuery(id+"F0.wireOp",EDGE,"E507"),sQuery(id+"F0.wireOp",EDGE,"E508"),sQuery(id+"F0.wireOp",EDGE,"E509"),sQuery(id+"F0.wireOp",EDGE,"E510"),sQuery(id+"F0.wireOp",EDGE,"E511"),sQuery(id+"F0.wireOp",EDGE,"E512"),sQuery(id+"F0.wireOp",EDGE,"E513"),sQuery(id+"F0.wireOp",EDGE,"E514"),sQuery(id+"F0.wireOp",EDGE,"E515"),sQuery(id+"F0.wireOp",EDGE,"E516"),sQuery(id+"F0.wireOp",EDGE,"E517"),sQuery(id+"F0.wireOp",EDGE,"E518"),sQuery(id+"F0.wireOp",EDGE,"E519"),sQuery(id+"F0.wireOp",EDGE,"E520"),sQuery(id+"F0.wireOp",EDGE,"E521"),sQuery(id+"F0.wireOp",EDGE,"E522"),sQuery(id+"F0.wireOp",EDGE,"E523"),sQuery(id+"F0.wireOp",EDGE,"E524"),sQuery(id+"F0.wireOp",EDGE,"E525"),sQuery(id+"F0.wireOp",EDGE,"E526"),sQuery(id+"F0.wireOp",EDGE,"E527"),sQuery(id+"F0.wireOp",EDGE,"E528"),sQuery(id+"F0.wireOp",EDGE,"E529"),sQuery(id+"F0.wireOp",EDGE,"E530"),sQuery(id+"F0.wireOp",EDGE,"E531"),sQuery(id+"F0.wireOp",EDGE,"E532"),sQuery(id+"F0.wireOp",EDGE,"E533"),sQuery(id+"F0.wireOp",EDGE,"E534"),sQuery(id+"F0.wireOp",EDGE,"E535"),sQuery(id+"F0.wireOp",EDGE,"E536"),sQuery(id+"F0.wireOp",EDGE,"E537"),sQuery(id+"F0.wireOp",EDGE,"E538"),sQuery(id+"F0.wireOp",EDGE,"E539"),sQuery(id+"F0.wireOp",EDGE,"E540"),sQuery(id+"F0.wireOp",EDGE,"E541"),sQuery(id+"F0.wireOp",EDGE,"E542"),sQuery(id+"F0.wireOp",EDGE,"E543"),sQuery(id+"F0.wireOp",EDGE,"E544"),sQuery(id+"F0.wireOp",EDGE,"E545"),sQuery(id+"F0.wireOp",EDGE,"E546"),sQuery(id+"F0.wireOp",EDGE,"E547"),sQuery(id+"F0.wireOp",EDGE,"E548"),sQuery(id+"F0.wireOp",EDGE,"E549"),sQuery(id+"F0.wireOp",EDGE,"E550"),sQuery(id+"F0.wireOp",EDGE,"E551"),sQuery(id+"F0.wireOp",EDGE,"E552"),sQuery(id+"F0.wireOp",EDGE,"E553"),sQuery(id+"F0.wireOp",EDGE,"E554"),sQuery(id+"F0.wireOp",EDGE,"E555"),sQuery(id+"F0.wireOp",EDGE,"E556"),sQuery(id+"F0.wireOp",EDGE,"E557"),sQuery(id+"F0.wireOp",EDGE,"E558"),sQuery(id+"F0.wireOp",EDGE,"E559"),sQuery(id+"F0.wireOp",EDGE,"E560"),sQuery(id+"F0.wireOp",EDGE,"E561"),sQuery(id+"F0.wireOp",EDGE,"E562"),sQuery(id+"F0.wireOp",EDGE,"E563"),sQuery(id+"F0.wireOp",EDGE,"E564"),sQuery(id+"F0.wireOp",EDGE,"E565"),sQuery(id+"F0.wireOp",EDGE,"E566"),sQuery(id+"F0.wireOp",EDGE,"E567"),sQuery(id+"F0.wireOp",EDGE,"E568"),sQuery(id+"F0.wireOp",EDGE,"E569"),sQuery(id+"F0.wireOp",EDGE,"E570"),sQuery(id+"F0.wireOp",EDGE,"E571"),sQuery(id+"F0.wireOp",EDGE,"E572"),sQuery(id+"F0.wireOp",EDGE,"E573"),sQuery(id+"F0.wireOp",EDGE,"E574"),sQuery(id+"F0.wireOp",EDGE,"E575"),sQuery(id+"F0.wireOp",EDGE,"E576"),sQuery(id+"F0.wireOp",EDGE,"E577"),sQuery(id+"F0.wireOp",EDGE,"E578"),sQuery(id+"F0.wireOp",EDGE,"E579"),sQuery(id+"F0.wireOp",EDGE,"E580"),sQuery(id+"F0.wireOp",EDGE,"E581"),sQuery(id+"F0.wireOp",EDGE,"E582"),sQuery(id+"F0.wireOp",EDGE,"E583"),sQuery(id+"F0.wireOp",EDGE,"E584"),sQuery(id+"F0.wireOp",EDGE,"E585"),sQuery(id+"F0.wireOp",EDGE,"E586"),sQuery(id+"F0.wireOp",EDGE,"E587"),sQuery(id+"F0.wireOp",EDGE,"E588"),sQuery(id+"F0.wireOp",EDGE,"E589"),sQuery(id+"F0.wireOp",EDGE,"E590"),sQuery(id+"F0.wireOp",EDGE,"E591"),sQuery(id+"F0.wireOp",EDGE,"E592"),sQuery(id+"F0.wireOp",EDGE,"E593"),sQuery(id+"F0.wireOp",EDGE,"E594"),sQuery(id+"F0.wireOp",EDGE,"E595"),sQuery(id+"F0.wireOp",EDGE,"E596"),sQuery(id+"F0.wireOp",EDGE,"E597"),sQuery(id+"F0.wireOp",EDGE,"E598"),sQuery(id+"F0.wireOp",EDGE,"E599"),sQuery(id+"F0.wireOp",EDGE,"E600"),sQuery(id+"F0.wireOp",EDGE,"E601"),sQuery(id+"F0.wireOp",EDGE,"E602"),sQuery(id+"F0.wireOp",EDGE,"E603"),sQuery(id+"F0.wireOp",EDGE,"E604"),sQuery(id+"F0.wireOp",EDGE,"E605"),sQuery(id+"F0.wireOp",EDGE,"E606"),sQuery(id+"F0.wireOp",EDGE,"E607"),sQuery(id+"F0.wireOp",EDGE,"E608"),sQuery(id+"F0.wireOp",EDGE,"E609")])],"isStart":false});
            var sketch = newSketch(context, id + "F2", { "sketchPlane" : qUnion([Q0])});
            skPoint(sketch, "E610.0", {"position": v(-31.05, 1.9) * mm});
            skPoint(sketch, "E611.0", {"position": v(-33.4, -1) * mm});
            skPoint(sketch, "E612.0", {"position": v(-30.05, -1.17) * mm});
            skPoint(sketch, "E613.0", {"position": v(15, 1.68) * mm});
            skPoint(sketch, "E614.0", {"position": v(17.95, -0.72) * mm});
            skPoint(sketch, "E615.0", {"position": v(14.3, -0.9) * mm});
            skCircle(sketch, "E616", {"center": v(16.08, 0) * mm, "radius": 2 * mm, "construction": true});
            skPoint(sketch, "E616.first.point", {"position": v(14.53, -1.26) * mm});
            skPoint(sketch, "E616.second.point", {"position": v(15.37, 1.87) * mm});
            skPoint(sketch, "E616.third.point", {"position": v(17.76, -1.09) * mm});
            skCircle(sketch, "E617", {"center": v(-31.67, 0) * mm, "radius": 2 * mm, "construction": true});
            skSolve(sketch);
        }
        {
            var Q0;
            Q0=makeQuery(id+"F1.opExtrude","SWEPT_BODY",BODY,{"disambiguationData":[OSD([sQuery(id+"F0.wireOp",EDGE,"E0"),sQuery(id+"F0.wireOp",EDGE,"E1"),sQuery(id+"F0.wireOp",EDGE,"E2"),sQuery(id+"F0.wireOp",EDGE,"E3"),sQuery(id+"F0.wireOp",EDGE,"E4"),sQuery(id+"F0.wireOp",EDGE,"E5"),sQuery(id+"F0.wireOp",EDGE,"E6"),sQuery(id+"F0.wireOp",EDGE,"E7"),sQuery(id+"F0.wireOp",EDGE,"E8"),sQuery(id+"F0.wireOp",EDGE,"E9"),sQuery(id+"F0.wireOp",EDGE,"E10"),sQuery(id+"F0.wireOp",EDGE,"E11"),sQuery(id+"F0.wireOp",EDGE,"E12"),sQuery(id+"F0.wireOp",EDGE,"E13"),sQuery(id+"F0.wireOp",EDGE,"E14"),sQuery(id+"F0.wireOp",EDGE,"E15"),sQuery(id+"F0.wireOp",EDGE,"E16"),sQuery(id+"F0.wireOp",EDGE,"E17"),sQuery(id+"F0.wireOp",EDGE,"E18"),sQuery(id+"F0.wireOp",EDGE,"E19"),sQuery(id+"F0.wireOp",EDGE,"E20"),sQuery(id+"F0.wireOp",EDGE,"E21"),sQuery(id+"F0.wireOp",EDGE,"E22"),sQuery(id+"F0.wireOp",EDGE,"E23"),sQuery(id+"F0.wireOp",EDGE,"E24"),sQuery(id+"F0.wireOp",EDGE,"E25"),sQuery(id+"F0.wireOp",EDGE,"E26"),sQuery(id+"F0.wireOp",EDGE,"E27"),sQuery(id+"F0.wireOp",EDGE,"E28"),sQuery(id+"F0.wireOp",EDGE,"E29"),sQuery(id+"F0.wireOp",EDGE,"E30"),sQuery(id+"F0.wireOp",EDGE,"E31"),sQuery(id+"F0.wireOp",EDGE,"E32"),sQuery(id+"F0.wireOp",EDGE,"E33"),sQuery(id+"F0.wireOp",EDGE,"E34"),sQuery(id+"F0.wireOp",EDGE,"E35"),sQuery(id+"F0.wireOp",EDGE,"E36"),sQuery(id+"F0.wireOp",EDGE,"E37"),sQuery(id+"F0.wireOp",EDGE,"E38"),sQuery(id+"F0.wireOp",EDGE,"E39"),sQuery(id+"F0.wireOp",EDGE,"E40"),sQuery(id+"F0.wireOp",EDGE,"E41"),sQuery(id+"F0.wireOp",EDGE,"E42"),sQuery(id+"F0.wireOp",EDGE,"E43"),sQuery(id+"F0.wireOp",EDGE,"E44"),sQuery(id+"F0.wireOp",EDGE,"E45"),sQuery(id+"F0.wireOp",EDGE,"E46"),sQuery(id+"F0.wireOp",EDGE,"E47"),sQuery(id+"F0.wireOp",EDGE,"E48"),sQuery(id+"F0.wireOp",EDGE,"E49"),sQuery(id+"F0.wireOp",EDGE,"E50"),sQuery(id+"F0.wireOp",EDGE,"E51"),sQuery(id+"F0.wireOp",EDGE,"E52"),sQuery(id+"F0.wireOp",EDGE,"E53"),sQuery(id+"F0.wireOp",EDGE,"E54"),sQuery(id+"F0.wireOp",EDGE,"E55"),sQuery(id+"F0.wireOp",EDGE,"E56"),sQuery(id+"F0.wireOp",EDGE,"E57"),sQuery(id+"F0.wireOp",EDGE,"E58"),sQuery(id+"F0.wireOp",EDGE,"E59"),sQuery(id+"F0.wireOp",EDGE,"E60"),sQuery(id+"F0.wireOp",EDGE,"E61"),sQuery(id+"F0.wireOp",EDGE,"E62"),sQuery(id+"F0.wireOp",EDGE,"E63"),sQuery(id+"F0.wireOp",EDGE,"E64"),sQuery(id+"F0.wireOp",EDGE,"E65"),sQuery(id+"F0.wireOp",EDGE,"E66"),sQuery(id+"F0.wireOp",EDGE,"E67"),sQuery(id+"F0.wireOp",EDGE,"E68"),sQuery(id+"F0.wireOp",EDGE,"E69"),sQuery(id+"F0.wireOp",EDGE,"E70"),sQuery(id+"F0.wireOp",EDGE,"E71"),sQuery(id+"F0.wireOp",EDGE,"E72"),sQuery(id+"F0.wireOp",EDGE,"E73"),sQuery(id+"F0.wireOp",EDGE,"E74"),sQuery(id+"F0.wireOp",EDGE,"E75"),sQuery(id+"F0.wireOp",EDGE,"E76"),sQuery(id+"F0.wireOp",EDGE,"E77"),sQuery(id+"F0.wireOp",EDGE,"E78"),sQuery(id+"F0.wireOp",EDGE,"E79"),sQuery(id+"F0.wireOp",EDGE,"E80"),sQuery(id+"F0.wireOp",EDGE,"E81"),sQuery(id+"F0.wireOp",EDGE,"E82"),sQuery(id+"F0.wireOp",EDGE,"E83"),sQuery(id+"F0.wireOp",EDGE,"E84"),sQuery(id+"F0.wireOp",EDGE,"E85"),sQuery(id+"F0.wireOp",EDGE,"E86"),sQuery(id+"F0.wireOp",EDGE,"E87"),sQuery(id+"F0.wireOp",EDGE,"E88"),sQuery(id+"F0.wireOp",EDGE,"E89"),sQuery(id+"F0.wireOp",EDGE,"E90"),sQuery(id+"F0.wireOp",EDGE,"E91"),sQuery(id+"F0.wireOp",EDGE,"E92"),sQuery(id+"F0.wireOp",EDGE,"E93"),sQuery(id+"F0.wireOp",EDGE,"E94"),sQuery(id+"F0.wireOp",EDGE,"E95"),sQuery(id+"F0.wireOp",EDGE,"E96"),sQuery(id+"F0.wireOp",EDGE,"E97"),sQuery(id+"F0.wireOp",EDGE,"E98"),sQuery(id+"F0.wireOp",EDGE,"E99"),sQuery(id+"F0.wireOp",EDGE,"E100"),sQuery(id+"F0.wireOp",EDGE,"E101"),sQuery(id+"F0.wireOp",EDGE,"E102"),sQuery(id+"F0.wireOp",EDGE,"E103"),sQuery(id+"F0.wireOp",EDGE,"E104"),sQuery(id+"F0.wireOp",EDGE,"E105"),sQuery(id+"F0.wireOp",EDGE,"E106"),sQuery(id+"F0.wireOp",EDGE,"E107"),sQuery(id+"F0.wireOp",EDGE,"E108"),sQuery(id+"F0.wireOp",EDGE,"E109"),sQuery(id+"F0.wireOp",EDGE,"E110"),sQuery(id+"F0.wireOp",EDGE,"E111"),sQuery(id+"F0.wireOp",EDGE,"E112"),sQuery(id+"F0.wireOp",EDGE,"E113"),sQuery(id+"F0.wireOp",EDGE,"E114"),sQuery(id+"F0.wireOp",EDGE,"E115"),sQuery(id+"F0.wireOp",EDGE,"E116"),sQuery(id+"F0.wireOp",EDGE,"E117"),sQuery(id+"F0.wireOp",EDGE,"E118"),sQuery(id+"F0.wireOp",EDGE,"E119"),sQuery(id+"F0.wireOp",EDGE,"E120"),sQuery(id+"F0.wireOp",EDGE,"E121"),sQuery(id+"F0.wireOp",EDGE,"E122"),sQuery(id+"F0.wireOp",EDGE,"E123"),sQuery(id+"F0.wireOp",EDGE,"E124"),sQuery(id+"F0.wireOp",EDGE,"E125"),sQuery(id+"F0.wireOp",EDGE,"E126"),sQuery(id+"F0.wireOp",EDGE,"E127"),sQuery(id+"F0.wireOp",EDGE,"E128"),sQuery(id+"F0.wireOp",EDGE,"E129"),sQuery(id+"F0.wireOp",EDGE,"E130"),sQuery(id+"F0.wireOp",EDGE,"E131"),sQuery(id+"F0.wireOp",EDGE,"E132"),sQuery(id+"F0.wireOp",EDGE,"E133"),sQuery(id+"F0.wireOp",EDGE,"E134"),sQuery(id+"F0.wireOp",EDGE,"E135"),sQuery(id+"F0.wireOp",EDGE,"E136"),sQuery(id+"F0.wireOp",EDGE,"E137"),sQuery(id+"F0.wireOp",EDGE,"E138"),sQuery(id+"F0.wireOp",EDGE,"E139"),sQuery(id+"F0.wireOp",EDGE,"E140"),sQuery(id+"F0.wireOp",EDGE,"E141"),sQuery(id+"F0.wireOp",EDGE,"E142"),sQuery(id+"F0.wireOp",EDGE,"E143"),sQuery(id+"F0.wireOp",EDGE,"E144"),sQuery(id+"F0.wireOp",EDGE,"E145"),sQuery(id+"F0.wireOp",EDGE,"E146"),sQuery(id+"F0.wireOp",EDGE,"E147"),sQuery(id+"F0.wireOp",EDGE,"E148"),sQuery(id+"F0.wireOp",EDGE,"E149"),sQuery(id+"F0.wireOp",EDGE,"E150"),sQuery(id+"F0.wireOp",EDGE,"E151"),sQuery(id+"F0.wireOp",EDGE,"E152"),sQuery(id+"F0.wireOp",EDGE,"E153"),sQuery(id+"F0.wireOp",EDGE,"E154"),sQuery(id+"F0.wireOp",EDGE,"E155"),sQuery(id+"F0.wireOp",EDGE,"E156"),sQuery(id+"F0.wireOp",EDGE,"E157"),sQuery(id+"F0.wireOp",EDGE,"E158"),sQuery(id+"F0.wireOp",EDGE,"E159"),sQuery(id+"F0.wireOp",EDGE,"E160"),sQuery(id+"F0.wireOp",EDGE,"E161"),sQuery(id+"F0.wireOp",EDGE,"E162"),sQuery(id+"F0.wireOp",EDGE,"E163"),sQuery(id+"F0.wireOp",EDGE,"E164"),sQuery(id+"F0.wireOp",EDGE,"E165"),sQuery(id+"F0.wireOp",EDGE,"E166"),sQuery(id+"F0.wireOp",EDGE,"E167"),sQuery(id+"F0.wireOp",EDGE,"E168"),sQuery(id+"F0.wireOp",EDGE,"E169"),sQuery(id+"F0.wireOp",EDGE,"E170"),sQuery(id+"F0.wireOp",EDGE,"E171"),sQuery(id+"F0.wireOp",EDGE,"E172"),sQuery(id+"F0.wireOp",EDGE,"E173"),sQuery(id+"F0.wireOp",EDGE,"E174"),sQuery(id+"F0.wireOp",EDGE,"E175"),sQuery(id+"F0.wireOp",EDGE,"E176"),sQuery(id+"F0.wireOp",EDGE,"E177"),sQuery(id+"F0.wireOp",EDGE,"E178"),sQuery(id+"F0.wireOp",EDGE,"E179"),sQuery(id+"F0.wireOp",EDGE,"E180"),sQuery(id+"F0.wireOp",EDGE,"E181"),sQuery(id+"F0.wireOp",EDGE,"E182"),sQuery(id+"F0.wireOp",EDGE,"E183"),sQuery(id+"F0.wireOp",EDGE,"E184"),sQuery(id+"F0.wireOp",EDGE,"E185"),sQuery(id+"F0.wireOp",EDGE,"E186"),sQuery(id+"F0.wireOp",EDGE,"E187"),sQuery(id+"F0.wireOp",EDGE,"E188"),sQuery(id+"F0.wireOp",EDGE,"E189"),sQuery(id+"F0.wireOp",EDGE,"E190"),sQuery(id+"F0.wireOp",EDGE,"E191"),sQuery(id+"F0.wireOp",EDGE,"E192"),sQuery(id+"F0.wireOp",EDGE,"E193"),sQuery(id+"F0.wireOp",EDGE,"E194"),sQuery(id+"F0.wireOp",EDGE,"E195"),sQuery(id+"F0.wireOp",EDGE,"E196"),sQuery(id+"F0.wireOp",EDGE,"E197"),sQuery(id+"F0.wireOp",EDGE,"E198"),sQuery(id+"F0.wireOp",EDGE,"E199")])]});
            var Q1;
            Q1=makeQuery(id+"F1.opExtrude","SWEPT_BODY",BODY,{"disambiguationData":[OSD([sQuery(id+"F0.wireOp",EDGE,"E200"),sQuery(id+"F0.wireOp",EDGE,"E201"),sQuery(id+"F0.wireOp",EDGE,"E202"),sQuery(id+"F0.wireOp",EDGE,"E203"),sQuery(id+"F0.wireOp",EDGE,"E204"),sQuery(id+"F0.wireOp",EDGE,"E205"),sQuery(id+"F0.wireOp",EDGE,"E206"),sQuery(id+"F0.wireOp",EDGE,"E207"),sQuery(id+"F0.wireOp",EDGE,"E208"),sQuery(id+"F0.wireOp",EDGE,"E209"),sQuery(id+"F0.wireOp",EDGE,"E210"),sQuery(id+"F0.wireOp",EDGE,"E211"),sQuery(id+"F0.wireOp",EDGE,"E212"),sQuery(id+"F0.wireOp",EDGE,"E213"),sQuery(id+"F0.wireOp",EDGE,"E214"),sQuery(id+"F0.wireOp",EDGE,"E215"),sQuery(id+"F0.wireOp",EDGE,"E216"),sQuery(id+"F0.wireOp",EDGE,"E217"),sQuery(id+"F0.wireOp",EDGE,"E218"),sQuery(id+"F0.wireOp",EDGE,"E219"),sQuery(id+"F0.wireOp",EDGE,"E220"),sQuery(id+"F0.wireOp",EDGE,"E221"),sQuery(id+"F0.wireOp",EDGE,"E222"),sQuery(id+"F0.wireOp",EDGE,"E223"),sQuery(id+"F0.wireOp",EDGE,"E224"),sQuery(id+"F0.wireOp",EDGE,"E225"),sQuery(id+"F0.wireOp",EDGE,"E226"),sQuery(id+"F0.wireOp",EDGE,"E227"),sQuery(id+"F0.wireOp",EDGE,"E228"),sQuery(id+"F0.wireOp",EDGE,"E229"),sQuery(id+"F0.wireOp",EDGE,"E230"),sQuery(id+"F0.wireOp",EDGE,"E231"),sQuery(id+"F0.wireOp",EDGE,"E232"),sQuery(id+"F0.wireOp",EDGE,"E233"),sQuery(id+"F0.wireOp",EDGE,"E234"),sQuery(id+"F0.wireOp",EDGE,"E235"),sQuery(id+"F0.wireOp",EDGE,"E236"),sQuery(id+"F0.wireOp",EDGE,"E237"),sQuery(id+"F0.wireOp",EDGE,"E238"),sQuery(id+"F0.wireOp",EDGE,"E239"),sQuery(id+"F0.wireOp",EDGE,"E240"),sQuery(id+"F0.wireOp",EDGE,"E241"),sQuery(id+"F0.wireOp",EDGE,"E242"),sQuery(id+"F0.wireOp",EDGE,"E243"),sQuery(id+"F0.wireOp",EDGE,"E244"),sQuery(id+"F0.wireOp",EDGE,"E245"),sQuery(id+"F0.wireOp",EDGE,"E246"),sQuery(id+"F0.wireOp",EDGE,"E247"),sQuery(id+"F0.wireOp",EDGE,"E248"),sQuery(id+"F0.wireOp",EDGE,"E249"),sQuery(id+"F0.wireOp",EDGE,"E250"),sQuery(id+"F0.wireOp",EDGE,"E251"),sQuery(id+"F0.wireOp",EDGE,"E252"),sQuery(id+"F0.wireOp",EDGE,"E253"),sQuery(id+"F0.wireOp",EDGE,"E254"),sQuery(id+"F0.wireOp",EDGE,"E255"),sQuery(id+"F0.wireOp",EDGE,"E256"),sQuery(id+"F0.wireOp",EDGE,"E257"),sQuery(id+"F0.wireOp",EDGE,"E258"),sQuery(id+"F0.wireOp",EDGE,"E259"),sQuery(id+"F0.wireOp",EDGE,"E260"),sQuery(id+"F0.wireOp",EDGE,"E261"),sQuery(id+"F0.wireOp",EDGE,"E262"),sQuery(id+"F0.wireOp",EDGE,"E263"),sQuery(id+"F0.wireOp",EDGE,"E264"),sQuery(id+"F0.wireOp",EDGE,"E265"),sQuery(id+"F0.wireOp",EDGE,"E266"),sQuery(id+"F0.wireOp",EDGE,"E267"),sQuery(id+"F0.wireOp",EDGE,"E268"),sQuery(id+"F0.wireOp",EDGE,"E269"),sQuery(id+"F0.wireOp",EDGE,"E270"),sQuery(id+"F0.wireOp",EDGE,"E271"),sQuery(id+"F0.wireOp",EDGE,"E272"),sQuery(id+"F0.wireOp",EDGE,"E273"),sQuery(id+"F0.wireOp",EDGE,"E274"),sQuery(id+"F0.wireOp",EDGE,"E275"),sQuery(id+"F0.wireOp",EDGE,"E276"),sQuery(id+"F0.wireOp",EDGE,"E277"),sQuery(id+"F0.wireOp",EDGE,"E278"),sQuery(id+"F0.wireOp",EDGE,"E279"),sQuery(id+"F0.wireOp",EDGE,"E280"),sQuery(id+"F0.wireOp",EDGE,"E281"),sQuery(id+"F0.wireOp",EDGE,"E282"),sQuery(id+"F0.wireOp",EDGE,"E283"),sQuery(id+"F0.wireOp",EDGE,"E284"),sQuery(id+"F0.wireOp",EDGE,"E285"),sQuery(id+"F0.wireOp",EDGE,"E286"),sQuery(id+"F0.wireOp",EDGE,"E287"),sQuery(id+"F0.wireOp",EDGE,"E288"),sQuery(id+"F0.wireOp",EDGE,"E289"),sQuery(id+"F0.wireOp",EDGE,"E290"),sQuery(id+"F0.wireOp",EDGE,"E291"),sQuery(id+"F0.wireOp",EDGE,"E292"),sQuery(id+"F0.wireOp",EDGE,"E293"),sQuery(id+"F0.wireOp",EDGE,"E294"),sQuery(id+"F0.wireOp",EDGE,"E295"),sQuery(id+"F0.wireOp",EDGE,"E296"),sQuery(id+"F0.wireOp",EDGE,"E297"),sQuery(id+"F0.wireOp",EDGE,"E298"),sQuery(id+"F0.wireOp",EDGE,"E299"),sQuery(id+"F0.wireOp",EDGE,"E300"),sQuery(id+"F0.wireOp",EDGE,"E301"),sQuery(id+"F0.wireOp",EDGE,"E302"),sQuery(id+"F0.wireOp",EDGE,"E303"),sQuery(id+"F0.wireOp",EDGE,"E304"),sQuery(id+"F0.wireOp",EDGE,"E305"),sQuery(id+"F0.wireOp",EDGE,"E306"),sQuery(id+"F0.wireOp",EDGE,"E307"),sQuery(id+"F0.wireOp",EDGE,"E308"),sQuery(id+"F0.wireOp",EDGE,"E309"),sQuery(id+"F0.wireOp",EDGE,"E310"),sQuery(id+"F0.wireOp",EDGE,"E311"),sQuery(id+"F0.wireOp",EDGE,"E312"),sQuery(id+"F0.wireOp",EDGE,"E313"),sQuery(id+"F0.wireOp",EDGE,"E314"),sQuery(id+"F0.wireOp",EDGE,"E315"),sQuery(id+"F0.wireOp",EDGE,"E316"),sQuery(id+"F0.wireOp",EDGE,"E317"),sQuery(id+"F0.wireOp",EDGE,"E318"),sQuery(id+"F0.wireOp",EDGE,"E319"),sQuery(id+"F0.wireOp",EDGE,"E320"),sQuery(id+"F0.wireOp",EDGE,"E321"),sQuery(id+"F0.wireOp",EDGE,"E322"),sQuery(id+"F0.wireOp",EDGE,"E323"),sQuery(id+"F0.wireOp",EDGE,"E324"),sQuery(id+"F0.wireOp",EDGE,"E325"),sQuery(id+"F0.wireOp",EDGE,"E326"),sQuery(id+"F0.wireOp",EDGE,"E327"),sQuery(id+"F0.wireOp",EDGE,"E328"),sQuery(id+"F0.wireOp",EDGE,"E329"),sQuery(id+"F0.wireOp",EDGE,"E330"),sQuery(id+"F0.wireOp",EDGE,"E331"),sQuery(id+"F0.wireOp",EDGE,"E332"),sQuery(id+"F0.wireOp",EDGE,"E333"),sQuery(id+"F0.wireOp",EDGE,"E334"),sQuery(id+"F0.wireOp",EDGE,"E335"),sQuery(id+"F0.wireOp",EDGE,"E336"),sQuery(id+"F0.wireOp",EDGE,"E337"),sQuery(id+"F0.wireOp",EDGE,"E338"),sQuery(id+"F0.wireOp",EDGE,"E339"),sQuery(id+"F0.wireOp",EDGE,"E340"),sQuery(id+"F0.wireOp",EDGE,"E341"),sQuery(id+"F0.wireOp",EDGE,"E342"),sQuery(id+"F0.wireOp",EDGE,"E343"),sQuery(id+"F0.wireOp",EDGE,"E344"),sQuery(id+"F0.wireOp",EDGE,"E345"),sQuery(id+"F0.wireOp",EDGE,"E346"),sQuery(id+"F0.wireOp",EDGE,"E347"),sQuery(id+"F0.wireOp",EDGE,"E348"),sQuery(id+"F0.wireOp",EDGE,"E349"),sQuery(id+"F0.wireOp",EDGE,"E350"),sQuery(id+"F0.wireOp",EDGE,"E351"),sQuery(id+"F0.wireOp",EDGE,"E352"),sQuery(id+"F0.wireOp",EDGE,"E353"),sQuery(id+"F0.wireOp",EDGE,"E354"),sQuery(id+"F0.wireOp",EDGE,"E355"),sQuery(id+"F0.wireOp",EDGE,"E356"),sQuery(id+"F0.wireOp",EDGE,"E357"),sQuery(id+"F0.wireOp",EDGE,"E358"),sQuery(id+"F0.wireOp",EDGE,"E359"),sQuery(id+"F0.wireOp",EDGE,"E360"),sQuery(id+"F0.wireOp",EDGE,"E361"),sQuery(id+"F0.wireOp",EDGE,"E362"),sQuery(id+"F0.wireOp",EDGE,"E363"),sQuery(id+"F0.wireOp",EDGE,"E364"),sQuery(id+"F0.wireOp",EDGE,"E365"),sQuery(id+"F0.wireOp",EDGE,"E366"),sQuery(id+"F0.wireOp",EDGE,"E367"),sQuery(id+"F0.wireOp",EDGE,"E368"),sQuery(id+"F0.wireOp",EDGE,"E369"),sQuery(id+"F0.wireOp",EDGE,"E370"),sQuery(id+"F0.wireOp",EDGE,"E371"),sQuery(id+"F0.wireOp",EDGE,"E372"),sQuery(id+"F0.wireOp",EDGE,"E373"),sQuery(id+"F0.wireOp",EDGE,"E374"),sQuery(id+"F0.wireOp",EDGE,"E375"),sQuery(id+"F0.wireOp",EDGE,"E376"),sQuery(id+"F0.wireOp",EDGE,"E377"),sQuery(id+"F0.wireOp",EDGE,"E378"),sQuery(id+"F0.wireOp",EDGE,"E379"),sQuery(id+"F0.wireOp",EDGE,"E380"),sQuery(id+"F0.wireOp",EDGE,"E381"),sQuery(id+"F0.wireOp",EDGE,"E382"),sQuery(id+"F0.wireOp",EDGE,"E383"),sQuery(id+"F0.wireOp",EDGE,"E384"),sQuery(id+"F0.wireOp",EDGE,"E385"),sQuery(id+"F0.wireOp",EDGE,"E386"),sQuery(id+"F0.wireOp",EDGE,"E387"),sQuery(id+"F0.wireOp",EDGE,"E388"),sQuery(id+"F0.wireOp",EDGE,"E389"),sQuery(id+"F0.wireOp",EDGE,"E390"),sQuery(id+"F0.wireOp",EDGE,"E391"),sQuery(id+"F0.wireOp",EDGE,"E392"),sQuery(id+"F0.wireOp",EDGE,"E393"),sQuery(id+"F0.wireOp",EDGE,"E394"),sQuery(id+"F0.wireOp",EDGE,"E395"),sQuery(id+"F0.wireOp",EDGE,"E396"),sQuery(id+"F0.wireOp",EDGE,"E397"),sQuery(id+"F0.wireOp",EDGE,"E398"),sQuery(id+"F0.wireOp",EDGE,"E399"),sQuery(id+"F0.wireOp",EDGE,"E400"),sQuery(id+"F0.wireOp",EDGE,"E401"),sQuery(id+"F0.wireOp",EDGE,"E402"),sQuery(id+"F0.wireOp",EDGE,"E403"),sQuery(id+"F0.wireOp",EDGE,"E404"),sQuery(id+"F0.wireOp",EDGE,"E405"),sQuery(id+"F0.wireOp",EDGE,"E406"),sQuery(id+"F0.wireOp",EDGE,"E407"),sQuery(id+"F0.wireOp",EDGE,"E408"),sQuery(id+"F0.wireOp",EDGE,"E409"),sQuery(id+"F0.wireOp",EDGE,"E410"),sQuery(id+"F0.wireOp",EDGE,"E411"),sQuery(id+"F0.wireOp",EDGE,"E412"),sQuery(id+"F0.wireOp",EDGE,"E413"),sQuery(id+"F0.wireOp",EDGE,"E414"),sQuery(id+"F0.wireOp",EDGE,"E415"),sQuery(id+"F0.wireOp",EDGE,"E416"),sQuery(id+"F0.wireOp",EDGE,"E417"),sQuery(id+"F0.wireOp",EDGE,"E418"),sQuery(id+"F0.wireOp",EDGE,"E419"),sQuery(id+"F0.wireOp",EDGE,"E420"),sQuery(id+"F0.wireOp",EDGE,"E421"),sQuery(id+"F0.wireOp",EDGE,"E422"),sQuery(id+"F0.wireOp",EDGE,"E423"),sQuery(id+"F0.wireOp",EDGE,"E424"),sQuery(id+"F0.wireOp",EDGE,"E425"),sQuery(id+"F0.wireOp",EDGE,"E426"),sQuery(id+"F0.wireOp",EDGE,"E427"),sQuery(id+"F0.wireOp",EDGE,"E428"),sQuery(id+"F0.wireOp",EDGE,"E429"),sQuery(id+"F0.wireOp",EDGE,"E430"),sQuery(id+"F0.wireOp",EDGE,"E431"),sQuery(id+"F0.wireOp",EDGE,"E432"),sQuery(id+"F0.wireOp",EDGE,"E433"),sQuery(id+"F0.wireOp",EDGE,"E434"),sQuery(id+"F0.wireOp",EDGE,"E435"),sQuery(id+"F0.wireOp",EDGE,"E436"),sQuery(id+"F0.wireOp",EDGE,"E437"),sQuery(id+"F0.wireOp",EDGE,"E438"),sQuery(id+"F0.wireOp",EDGE,"E439"),sQuery(id+"F0.wireOp",EDGE,"E440"),sQuery(id+"F0.wireOp",EDGE,"E441"),sQuery(id+"F0.wireOp",EDGE,"E442"),sQuery(id+"F0.wireOp",EDGE,"E443"),sQuery(id+"F0.wireOp",EDGE,"E444"),sQuery(id+"F0.wireOp",EDGE,"E445"),sQuery(id+"F0.wireOp",EDGE,"E446"),sQuery(id+"F0.wireOp",EDGE,"E447"),sQuery(id+"F0.wireOp",EDGE,"E448"),sQuery(id+"F0.wireOp",EDGE,"E449"),sQuery(id+"F0.wireOp",EDGE,"E450"),sQuery(id+"F0.wireOp",EDGE,"E451"),sQuery(id+"F0.wireOp",EDGE,"E452"),sQuery(id+"F0.wireOp",EDGE,"E453"),sQuery(id+"F0.wireOp",EDGE,"E454"),sQuery(id+"F0.wireOp",EDGE,"E455"),sQuery(id+"F0.wireOp",EDGE,"E456"),sQuery(id+"F0.wireOp",EDGE,"E457"),sQuery(id+"F0.wireOp",EDGE,"E458"),sQuery(id+"F0.wireOp",EDGE,"E459"),sQuery(id+"F0.wireOp",EDGE,"E460"),sQuery(id+"F0.wireOp",EDGE,"E461"),sQuery(id+"F0.wireOp",EDGE,"E462"),sQuery(id+"F0.wireOp",EDGE,"E463"),sQuery(id+"F0.wireOp",EDGE,"E464"),sQuery(id+"F0.wireOp",EDGE,"E465"),sQuery(id+"F0.wireOp",EDGE,"E466"),sQuery(id+"F0.wireOp",EDGE,"E467"),sQuery(id+"F0.wireOp",EDGE,"E468"),sQuery(id+"F0.wireOp",EDGE,"E469"),sQuery(id+"F0.wireOp",EDGE,"E470"),sQuery(id+"F0.wireOp",EDGE,"E471"),sQuery(id+"F0.wireOp",EDGE,"E472"),sQuery(id+"F0.wireOp",EDGE,"E473"),sQuery(id+"F0.wireOp",EDGE,"E474"),sQuery(id+"F0.wireOp",EDGE,"E475"),sQuery(id+"F0.wireOp",EDGE,"E476"),sQuery(id+"F0.wireOp",EDGE,"E477"),sQuery(id+"F0.wireOp",EDGE,"E478"),sQuery(id+"F0.wireOp",EDGE,"E479"),sQuery(id+"F0.wireOp",EDGE,"E480"),sQuery(id+"F0.wireOp",EDGE,"E481"),sQuery(id+"F0.wireOp",EDGE,"E482"),sQuery(id+"F0.wireOp",EDGE,"E483"),sQuery(id+"F0.wireOp",EDGE,"E484"),sQuery(id+"F0.wireOp",EDGE,"E485"),sQuery(id+"F0.wireOp",EDGE,"E486"),sQuery(id+"F0.wireOp",EDGE,"E487"),sQuery(id+"F0.wireOp",EDGE,"E488"),sQuery(id+"F0.wireOp",EDGE,"E489"),sQuery(id+"F0.wireOp",EDGE,"E490"),sQuery(id+"F0.wireOp",EDGE,"E491"),sQuery(id+"F0.wireOp",EDGE,"E492"),sQuery(id+"F0.wireOp",EDGE,"E493"),sQuery(id+"F0.wireOp",EDGE,"E494"),sQuery(id+"F0.wireOp",EDGE,"E495"),sQuery(id+"F0.wireOp",EDGE,"E496"),sQuery(id+"F0.wireOp",EDGE,"E497"),sQuery(id+"F0.wireOp",EDGE,"E498"),sQuery(id+"F0.wireOp",EDGE,"E499"),sQuery(id+"F0.wireOp",EDGE,"E500"),sQuery(id+"F0.wireOp",EDGE,"E501"),sQuery(id+"F0.wireOp",EDGE,"E502"),sQuery(id+"F0.wireOp",EDGE,"E503"),sQuery(id+"F0.wireOp",EDGE,"E504"),sQuery(id+"F0.wireOp",EDGE,"E505"),sQuery(id+"F0.wireOp",EDGE,"E506"),sQuery(id+"F0.wireOp",EDGE,"E507"),sQuery(id+"F0.wireOp",EDGE,"E508"),sQuery(id+"F0.wireOp",EDGE,"E509"),sQuery(id+"F0.wireOp",EDGE,"E510"),sQuery(id+"F0.wireOp",EDGE,"E511"),sQuery(id+"F0.wireOp",EDGE,"E512"),sQuery(id+"F0.wireOp",EDGE,"E513"),sQuery(id+"F0.wireOp",EDGE,"E514"),sQuery(id+"F0.wireOp",EDGE,"E515"),sQuery(id+"F0.wireOp",EDGE,"E516"),sQuery(id+"F0.wireOp",EDGE,"E517"),sQuery(id+"F0.wireOp",EDGE,"E518"),sQuery(id+"F0.wireOp",EDGE,"E519"),sQuery(id+"F0.wireOp",EDGE,"E520"),sQuery(id+"F0.wireOp",EDGE,"E521"),sQuery(id+"F0.wireOp",EDGE,"E522"),sQuery(id+"F0.wireOp",EDGE,"E523"),sQuery(id+"F0.wireOp",EDGE,"E524"),sQuery(id+"F0.wireOp",EDGE,"E525"),sQuery(id+"F0.wireOp",EDGE,"E526"),sQuery(id+"F0.wireOp",EDGE,"E527"),sQuery(id+"F0.wireOp",EDGE,"E528"),sQuery(id+"F0.wireOp",EDGE,"E529"),sQuery(id+"F0.wireOp",EDGE,"E530"),sQuery(id+"F0.wireOp",EDGE,"E531"),sQuery(id+"F0.wireOp",EDGE,"E532"),sQuery(id+"F0.wireOp",EDGE,"E533"),sQuery(id+"F0.wireOp",EDGE,"E534"),sQuery(id+"F0.wireOp",EDGE,"E535"),sQuery(id+"F0.wireOp",EDGE,"E536"),sQuery(id+"F0.wireOp",EDGE,"E537"),sQuery(id+"F0.wireOp",EDGE,"E538"),sQuery(id+"F0.wireOp",EDGE,"E539"),sQuery(id+"F0.wireOp",EDGE,"E540"),sQuery(id+"F0.wireOp",EDGE,"E541"),sQuery(id+"F0.wireOp",EDGE,"E542"),sQuery(id+"F0.wireOp",EDGE,"E543"),sQuery(id+"F0.wireOp",EDGE,"E544"),sQuery(id+"F0.wireOp",EDGE,"E545"),sQuery(id+"F0.wireOp",EDGE,"E546"),sQuery(id+"F0.wireOp",EDGE,"E547"),sQuery(id+"F0.wireOp",EDGE,"E548"),sQuery(id+"F0.wireOp",EDGE,"E549"),sQuery(id+"F0.wireOp",EDGE,"E550"),sQuery(id+"F0.wireOp",EDGE,"E551"),sQuery(id+"F0.wireOp",EDGE,"E552"),sQuery(id+"F0.wireOp",EDGE,"E553"),sQuery(id+"F0.wireOp",EDGE,"E554"),sQuery(id+"F0.wireOp",EDGE,"E555"),sQuery(id+"F0.wireOp",EDGE,"E556"),sQuery(id+"F0.wireOp",EDGE,"E557"),sQuery(id+"F0.wireOp",EDGE,"E558"),sQuery(id+"F0.wireOp",EDGE,"E559"),sQuery(id+"F0.wireOp",EDGE,"E560"),sQuery(id+"F0.wireOp",EDGE,"E561"),sQuery(id+"F0.wireOp",EDGE,"E562"),sQuery(id+"F0.wireOp",EDGE,"E563"),sQuery(id+"F0.wireOp",EDGE,"E564"),sQuery(id+"F0.wireOp",EDGE,"E565"),sQuery(id+"F0.wireOp",EDGE,"E566"),sQuery(id+"F0.wireOp",EDGE,"E567"),sQuery(id+"F0.wireOp",EDGE,"E568"),sQuery(id+"F0.wireOp",EDGE,"E569"),sQuery(id+"F0.wireOp",EDGE,"E570"),sQuery(id+"F0.wireOp",EDGE,"E571"),sQuery(id+"F0.wireOp",EDGE,"E572"),sQuery(id+"F0.wireOp",EDGE,"E573"),sQuery(id+"F0.wireOp",EDGE,"E574"),sQuery(id+"F0.wireOp",EDGE,"E575"),sQuery(id+"F0.wireOp",EDGE,"E576"),sQuery(id+"F0.wireOp",EDGE,"E577"),sQuery(id+"F0.wireOp",EDGE,"E578"),sQuery(id+"F0.wireOp",EDGE,"E579"),sQuery(id+"F0.wireOp",EDGE,"E580"),sQuery(id+"F0.wireOp",EDGE,"E581"),sQuery(id+"F0.wireOp",EDGE,"E582"),sQuery(id+"F0.wireOp",EDGE,"E583"),sQuery(id+"F0.wireOp",EDGE,"E584"),sQuery(id+"F0.wireOp",EDGE,"E585"),sQuery(id+"F0.wireOp",EDGE,"E586"),sQuery(id+"F0.wireOp",EDGE,"E587"),sQuery(id+"F0.wireOp",EDGE,"E588"),sQuery(id+"F0.wireOp",EDGE,"E589"),sQuery(id+"F0.wireOp",EDGE,"E590"),sQuery(id+"F0.wireOp",EDGE,"E591"),sQuery(id+"F0.wireOp",EDGE,"E592"),sQuery(id+"F0.wireOp",EDGE,"E593"),sQuery(id+"F0.wireOp",EDGE,"E594"),sQuery(id+"F0.wireOp",EDGE,"E595"),sQuery(id+"F0.wireOp",EDGE,"E596"),sQuery(id+"F0.wireOp",EDGE,"E597"),sQuery(id+"F0.wireOp",EDGE,"E598"),sQuery(id+"F0.wireOp",EDGE,"E599"),sQuery(id+"F0.wireOp",EDGE,"E600"),sQuery(id+"F0.wireOp",EDGE,"E601"),sQuery(id+"F0.wireOp",EDGE,"E602"),sQuery(id+"F0.wireOp",EDGE,"E603"),sQuery(id+"F0.wireOp",EDGE,"E604"),sQuery(id+"F0.wireOp",EDGE,"E605"),sQuery(id+"F0.wireOp",EDGE,"E606"),sQuery(id+"F0.wireOp",EDGE,"E607"),sQuery(id+"F0.wireOp",EDGE,"E608"),sQuery(id+"F0.wireOp",EDGE,"E609")])]});
            var Q2;
            Q2=sQuery(id+"F2.wireOp",VERTEX,"E616.center");
            transform(context, id + "F3", {"entities" : qUnion([Q0, Q1]), "transformType" : TransformType.SCALE_UNIFORMLY, "scale" : 0.53, "scalePoint" : qUnion([Q2]), "makeCopy" : false});
        }
    });
